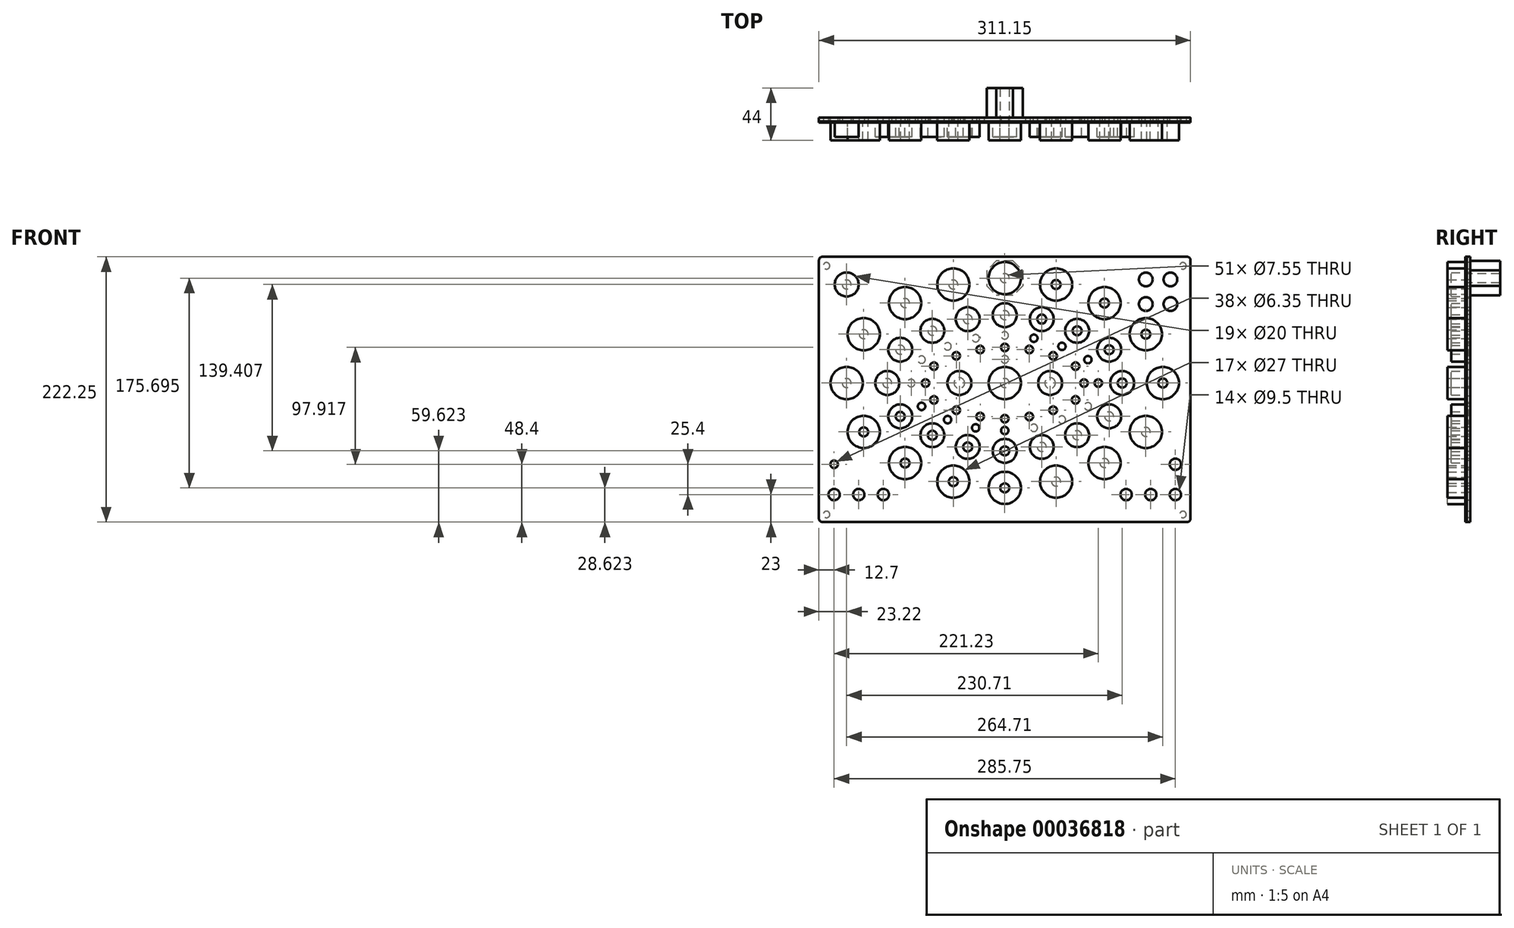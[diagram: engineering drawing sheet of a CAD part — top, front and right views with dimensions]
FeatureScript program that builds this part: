
annotation { "Feature Type Name" : "Feature", "Feature Type Description" : "" }
export const myFeature = defineFeature(function(context is Context, id is Id, definition is map)
    precondition{}
    {
        {
            var Q0;
            Q0=qCreatedBy(makeId("Front.planeOp"),FACE);
            var sketch = newSketch(context, id + "F0", { "sketchPlane" : qUnion([Q0])});
            skLineSegment(sketch, "E0.bottom", {"start": v(0, 0) * mm, "end": v(311.15, 0) * mm});
            skLineSegment(sketch, "E0.top", {"start": v(0, 222.25) * mm, "end": v(311.15, 222.25) * mm});
            skLineSegment(sketch, "E0.left", {"start": v(0, 0) * mm, "end": v(0, 222.25) * mm});
            skLineSegment(sketch, "E0.right", {"start": v(311.15, 0) * mm, "end": v(311.15, 222.25) * mm});
            skLineSegment(sketch, "E1", {"start": v(155.57, 222.25) * mm, "end": v(155.57, 0) * mm, "construction": true});
            skLineSegment(sketch, "E2", {"start": v(0, 116.47) * mm, "end": v(311.15, 116.47) * mm, "construction": true});
            skArc(sketch, "E3", {"start": v(50, 169.56) * mm, "mid": v(23.22, 116.47) * mm, "end": v(50, 63.38) * mm, "construction": true});
            skArc(sketch, "E4", {"start": v(261.14, 63.38) * mm, "mid": v(287.93, 116.47) * mm, "end": v(261.14, 169.56) * mm, "construction": true});
            skArc(sketch, "E5", {"start": v(50, 63.38) * mm, "mid": v(155.57, 28.62) * mm, "end": v(261.14, 63.38) * mm, "construction": true});
            skArc(sketch, "E6.trimOffspring", {"start": v(261.14, 169.56) * mm, "mid": v(155.57, 204.32) * mm, "end": v(50, 169.56) * mm, "construction": true});
            skPoint(sketch, "E7", {"position": v(23.22, 116.47) * mm});
            skPoint(sketch, "E8", {"position": v(287.93, 116.47) * mm});
            skPoint(sketch, "E9", {"position": v(155.57, 204.32) * mm});
            skPoint(sketch, "E10", {"position": v(155.57, 28.62) * mm});
            skLineSegment(sketch, "E11", {"start": v(23.22, 116.47) * mm, "end": v(37.45, 157.41) * mm, "construction": true});
            skLineSegment(sketch, "E12", {"start": v(72.09, 183.48) * mm, "end": v(37.45, 157.41) * mm, "construction": true});
            skLineSegment(sketch, "E13", {"start": v(72.09, 183.48) * mm, "end": v(112.55, 199.03) * mm, "construction": true});
            skLineSegment(sketch, "E14", {"start": v(155.57, 204.32) * mm, "end": v(112.55, 199.03) * mm, "construction": true});
            skLineSegment(sketch, "E15", {"start": v(112.55, 199.03) * mm, "end": v(72.09, 183.48) * mm, "construction": true});
            skCircle(sketch, "E16", {"center": v(23.22, 116.47) * mm, "radius": 3.78 * mm});
            skCircle(sketch, "E17", {"center": v(37.45, 157.41) * mm, "radius": 3.78 * mm});
            skCircle(sketch, "E18", {"center": v(72.09, 183.48) * mm, "radius": 3.78 * mm});
            skCircle(sketch, "E19", {"center": v(112.55, 199.03) * mm, "radius": 3.78 * mm});
            skCircle(sketch, "E20", {"center": v(155.57, 204.32) * mm, "radius": 3.78 * mm});
            skArc(sketch, "E21", {"start": v(242.72, 88.32) * mm, "mid": v(256.93, 116.47) * mm, "end": v(242.72, 144.62) * mm, "construction": true});
            skArc(sketch, "E22.trimOffspring", {"start": v(68.43, 144.62) * mm, "mid": v(54.22, 116.47) * mm, "end": v(68.43, 88.32) * mm, "construction": true});
            skArc(sketch, "E23.trimOffspring", {"start": v(242.72, 144.62) * mm, "mid": v(155.57, 173.32) * mm, "end": v(68.43, 144.62) * mm, "construction": true});
            skCircle(sketch, "E24", {"center": v(155.57, 173.32) * mm, "radius": 3.78 * mm});
            skCircle(sketch, "E25", {"center": v(124.57, 170) * mm, "radius": 3.78 * mm});
            skCircle(sketch, "E26", {"center": v(94.97, 160.21) * mm, "radius": 3.78 * mm});
            skArc(sketch, "E27", {"start": v(78.53, 130.95) * mm, "mid": v(71.22, 116.47) * mm, "end": v(78.53, 102) * mm, "construction": true});
            skArc(sketch, "E28", {"start": v(232.62, 102) * mm, "mid": v(239.93, 116.47) * mm, "end": v(232.62, 130.95) * mm, "construction": true});
            skArc(sketch, "E29.trimOffspring", {"start": v(232.62, 130.95) * mm, "mid": v(155.57, 156.32) * mm, "end": v(78.53, 130.95) * mm, "construction": true});
            skCircle(sketch, "E30", {"center": v(155.57, 156.32) * mm, "radius": 3.1 * mm});
            skCircle(sketch, "E31", {"center": v(131.21, 154) * mm, "radius": 3.1 * mm});
            skCircle(sketch, "E32", {"center": v(107.72, 147.16) * mm, "radius": 3.1 * mm});
            skLineSegment(sketch, "E33", {"start": v(107.72, 147.16) * mm, "end": v(131.21, 154) * mm, "construction": true});
            skLineSegment(sketch, "E34", {"start": v(131.21, 154) * mm, "end": v(155.57, 156.32) * mm, "construction": true});
            skLineSegment(sketch, "E35", {"start": v(94.97, 160.21) * mm, "end": v(124.57, 170) * mm, "construction": true});
            skLineSegment(sketch, "E36", {"start": v(124.57, 170) * mm, "end": v(155.57, 173.32) * mm, "construction": true});
            skCircle(sketch, "E37", {"center": v(54.22, 116.47) * mm, "radius": 3.78 * mm, "construction": true});
            skLineSegment(sketch, "E38", {"start": v(54.22, 116.47) * mm, "end": v(68.1, 144.39) * mm, "construction": true});
            skPoint(sketch, "E39.trimOffspring.end.orphan", {"position": v(311.15, 111.12) * mm});
            skArc(sketch, "E40", {"start": v(68.43, 88.32) * mm, "mid": v(155.57, 59.62) * mm, "end": v(242.72, 88.32) * mm, "construction": true});
            skArc(sketch, "E41", {"start": v(78.53, 102) * mm, "mid": v(155.57, 76.62) * mm, "end": v(232.62, 102) * mm, "construction": true});
            skCircle(sketch, "E42", {"center": v(71.22, 116.47) * mm, "radius": 3.1 * mm, "construction": true});
            skArc(sketch, "E43", {"start": v(84.47, 122.9) * mm, "mid": v(81.22, 116.47) * mm, "end": v(84.47, 110.03) * mm, "construction": true});
            skArc(sketch, "E44", {"start": v(226.68, 110.03) * mm, "mid": v(229.93, 116.47) * mm, "end": v(226.68, 122.9) * mm, "construction": true});
            skArc(sketch, "E45", {"start": v(226.68, 122.9) * mm, "mid": v(155.57, 146.32) * mm, "end": v(84.47, 122.9) * mm, "construction": true});
            skArc(sketch, "E46", {"start": v(84.47, 110.03) * mm, "mid": v(155.58, 86.62) * mm, "end": v(226.68, 110.03) * mm, "construction": true});
            skCircle(sketch, "E47", {"center": v(155.58, 146.32) * mm, "radius": 3.17 * mm});
            skCircle(sketch, "E48", {"center": v(81.22, 116.47) * mm, "radius": 3.17 * mm, "construction": true});
            skCircle(sketch, "E49", {"center": v(96.28, 130.6) * mm, "radius": 3.17 * mm});
            skCircle(sketch, "E50", {"center": v(115.04, 139.24) * mm, "radius": 3.17 * mm});
            skCircle(sketch, "E51", {"center": v(135, 144.54) * mm, "radius": 3.17 * mm});
            skLineSegment(sketch, "E52", {"start": v(155.58, 146.32) * mm, "end": v(135, 144.54) * mm, "construction": true});
            skLineSegment(sketch, "E53", {"start": v(135, 144.54) * mm, "end": v(115.04, 139.24) * mm, "construction": true});
            skLineSegment(sketch, "E54", {"start": v(115.04, 139.24) * mm, "end": v(96.28, 130.6) * mm, "construction": true});
            skLineSegment(sketch, "E55", {"start": v(96.28, 130.6) * mm, "end": v(81.22, 116.47) * mm, "construction": true});
            skLineSegment(sketch, "E56", {"start": v(68.1, 144.39) * mm, "end": v(94.97, 160.21) * mm, "construction": true});
            skCircle(sketch, "E57", {"center": v(68.1, 144.39) * mm, "radius": 3.78 * mm});
            skCircle(sketch, "E58", {"center": v(85.93, 136.03) * mm, "radius": 3.1 * mm});
            skLineSegment(sketch, "E59", {"start": v(71.22, 116.47) * mm, "end": v(85.93, 136.03) * mm, "construction": true});
            skLineSegment(sketch, "E60", {"start": v(107.72, 147.16) * mm, "end": v(85.93, 136.03) * mm, "construction": true});
            skCircle(sketch, "E61", {"center": v(117.57, 116.47) * mm, "radius": 4.45 * mm});
            skCircle(sketch, "E62", {"center": v(193.57, 116.47) * mm, "radius": 4.45 * mm});
            skCircle(sketch, "E63", {"center": v(155.58, 116.47) * mm, "radius": 3.78 * mm});
            skCircle(sketch, "E64", {"center": v(298.45, 23) * mm, "radius": 4.75 * mm});
            skCircle(sketch, "E65", {"center": v(298.45, 48.4) * mm, "radius": 4.75 * mm});
            skCircle(sketch, "E66", {"center": v(277.83, 23) * mm, "radius": 4.75 * mm});
            skCircle(sketch, "E67", {"center": v(257.2, 23) * mm, "radius": 4.75 * mm});
            skLineSegment(sketch, "E68", {"start": v(257.2, 23) * mm, "end": v(277.83, 23) * mm, "construction": true});
            skLineSegment(sketch, "E69", {"start": v(277.83, 23) * mm, "end": v(298.45, 23) * mm, "construction": true});
            skCircle(sketch, "E70.MirrorC", {"center": v(256.93, 116.47) * mm, "radius": 3.78 * mm, "construction": true});
            skCircle(sketch, "E71.MirrorC", {"center": v(243.04, 144.39) * mm, "radius": 3.78 * mm});
            skCircle(sketch, "E72.MirrorC", {"center": v(216.18, 160.21) * mm, "radius": 3.78 * mm});
            skCircle(sketch, "E73.MirrorC", {"center": v(186.58, 170) * mm, "radius": 3.78 * mm});
            skCircle(sketch, "E74.MirrorC", {"center": v(198.6, 199.03) * mm, "radius": 3.78 * mm});
            skCircle(sketch, "E75.MirrorC", {"center": v(239.06, 183.48) * mm, "radius": 3.78 * mm});
            skCircle(sketch, "E76.MirrorC", {"center": v(273.7, 157.41) * mm, "radius": 3.78 * mm});
            skCircle(sketch, "E77.MirrorC", {"center": v(287.93, 116.47) * mm, "radius": 3.78 * mm});
            skCircle(sketch, "E78.MirrorC", {"center": v(37.45, 75.53) * mm, "radius": 3.78 * mm});
            skCircle(sketch, "E79.MirrorC", {"center": v(72.09, 49.46) * mm, "radius": 3.78 * mm});
            skCircle(sketch, "E80.MirrorC", {"center": v(112.55, 33.9) * mm, "radius": 3.78 * mm});
            skCircle(sketch, "E81.MirrorC", {"center": v(155.57, 28.62) * mm, "radius": 3.78 * mm});
            skCircle(sketch, "E82.MirrorC", {"center": v(198.6, 33.9) * mm, "radius": 3.78 * mm});
            skCircle(sketch, "E83.MirrorC", {"center": v(239.06, 49.46) * mm, "radius": 3.78 * mm});
            skCircle(sketch, "E84.MirrorC", {"center": v(273.7, 75.53) * mm, "radius": 3.78 * mm});
            skCircle(sketch, "E85.MirrorC", {"center": v(243.04, 88.55) * mm, "radius": 3.78 * mm});
            skCircle(sketch, "E86.MirrorC", {"center": v(216.18, 72.73) * mm, "radius": 3.78 * mm});
            skCircle(sketch, "E87.MirrorC", {"center": v(186.58, 62.94) * mm, "radius": 3.78 * mm});
            skCircle(sketch, "E88.MirrorC", {"center": v(155.57, 59.62) * mm, "radius": 3.78 * mm});
            skCircle(sketch, "E89.MirrorC", {"center": v(124.57, 62.94) * mm, "radius": 3.78 * mm});
            skCircle(sketch, "E90.MirrorC", {"center": v(94.97, 72.73) * mm, "radius": 3.78 * mm});
            skCircle(sketch, "E91.MirrorC", {"center": v(68.1, 88.55) * mm, "radius": 3.78 * mm});
            skCircle(sketch, "E92.MirrorC", {"center": v(85.93, 96.91) * mm, "radius": 3.1 * mm});
            skCircle(sketch, "E93.MirrorC", {"center": v(107.72, 85.78) * mm, "radius": 3.1 * mm});
            skCircle(sketch, "E94.MirrorC", {"center": v(131.21, 78.93) * mm, "radius": 3.1 * mm});
            skCircle(sketch, "E95.MirrorC", {"center": v(155.57, 76.62) * mm, "radius": 3.1 * mm});
            skCircle(sketch, "E96.MirrorC", {"center": v(155.58, 86.62) * mm, "radius": 3.17 * mm});
            skCircle(sketch, "E97.MirrorC", {"center": v(135, 88.4) * mm, "radius": 3.17 * mm});
            skCircle(sketch, "E98.MirrorC", {"center": v(115.04, 93.7) * mm, "radius": 3.17 * mm});
            skCircle(sketch, "E99.MirrorC", {"center": v(96.28, 102.34) * mm, "radius": 3.17 * mm});
            skCircle(sketch, "E100.MirrorC", {"center": v(176.15, 144.54) * mm, "radius": 3.17 * mm});
            skCircle(sketch, "E101.MirrorC", {"center": v(179.94, 154) * mm, "radius": 3.1 * mm});
            skCircle(sketch, "E102.MirrorC", {"center": v(203.43, 147.16) * mm, "radius": 3.1 * mm});
            skCircle(sketch, "E103.MirrorC", {"center": v(196.11, 139.24) * mm, "radius": 3.17 * mm});
            skCircle(sketch, "E104.MirrorC", {"center": v(214.87, 130.6) * mm, "radius": 3.17 * mm});
            skCircle(sketch, "E105.MirrorC", {"center": v(225.22, 136.03) * mm, "radius": 3.1 * mm});
            skCircle(sketch, "E106.MirrorC", {"center": v(225.22, 96.91) * mm, "radius": 3.1 * mm});
            skCircle(sketch, "E107.MirrorC", {"center": v(203.43, 85.78) * mm, "radius": 3.1 * mm});
            skCircle(sketch, "E108.MirrorC", {"center": v(196.11, 93.7) * mm, "radius": 3.17 * mm});
            skCircle(sketch, "E109.MirrorC", {"center": v(176.15, 88.4) * mm, "radius": 3.17 * mm});
            skCircle(sketch, "E110.MirrorC", {"center": v(179.94, 78.93) * mm, "radius": 3.1 * mm});
            skCircle(sketch, "E111.MirrorC", {"center": v(239.93, 116.47) * mm, "radius": 3.1 * mm, "construction": true});
            skCircle(sketch, "E112.MirrorC", {"center": v(229.93, 116.47) * mm, "radius": 3.17 * mm, "construction": true});
            skCircle(sketch, "E113.MirrorC", {"center": v(33.32, 23) * mm, "radius": 4.75 * mm});
            skCircle(sketch, "E114.MirrorC", {"center": v(12.7, 23) * mm, "radius": 4.75 * mm});
            skCircle(sketch, "E115.MirrorC", {"center": v(12.7, 48.4) * mm, "radius": 4.75 * mm, "construction": true});
            skCircle(sketch, "E116.MirrorC", {"center": v(214.87, 102.34) * mm, "radius": 3.17 * mm});
            skCircle(sketch, "E117", {"center": v(89.22, 116.47) * mm, "radius": 3.17 * mm});
            skCircle(sketch, "E118", {"center": v(221.93, 116.47) * mm, "radius": 3.17 * mm});
            skCircle(sketch, "E119", {"center": v(294.32, 203.2) * mm, "radius": 5.75 * mm});
            skCircle(sketch, "E120", {"center": v(294.32, 182.58) * mm, "radius": 5.75 * mm});
            skCircle(sketch, "E121", {"center": v(273.7, 203.2) * mm, "radius": 5.75 * mm});
            skCircle(sketch, "E122", {"center": v(273.7, 182.58) * mm, "radius": 5.75 * mm});
            skCircle(sketch, "E123", {"center": v(23.22, 199.03) * mm, "radius": 3.78 * mm});
            skCircle(sketch, "E124", {"center": v(12.7, 48.4) * mm, "radius": 3.17 * mm});
            skCircle(sketch, "E125", {"center": v(155.58, 136.32) * mm, "radius": 3.17 * mm});
            skCircle(sketch, "E126", {"center": v(53.94, 23) * mm, "radius": 4.75 * mm});
            skCircle(sketch, "E127", {"center": v(236.59, 23) * mm, "radius": 4.75 * mm, "construction": true});
            skLineSegment(sketch, "E128", {"start": v(257.2, 23) * mm, "end": v(236.59, 23) * mm, "construction": true});
            skLineSegment(sketch, "E129", {"start": v(33.32, 23) * mm, "end": v(53.94, 23) * mm, "construction": true});
            skLineSegment(sketch, "E130", {"start": v(12.7, 23) * mm, "end": v(33.32, 23) * mm, "construction": true});
            skCircle(sketch, "E131", {"center": v(277.83, 48.4) * mm, "radius": 4.75 * mm, "construction": true});
            skCircle(sketch, "E132", {"center": v(77.22, 116.47) * mm, "radius": 3.17 * mm});
            skCircle(sketch, "E133", {"center": v(233.93, 116.47) * mm, "radius": 3.17 * mm});
            skLineSegment(sketch, "E134", {"start": v(273.7, 203.2) * mm, "end": v(294.32, 203.2) * mm, "construction": true});
            skCircle(sketch, "E135", {"center": v(273.7, 203.2) * mm, "radius": 6.5 * mm, "construction": true});
            skCircle(sketch, "E136", {"center": v(294.32, 203.2) * mm, "radius": 6.5 * mm, "construction": true});
            skCircle(sketch, "E137", {"center": v(294.32, 182.58) * mm, "radius": 6.5 * mm, "construction": true});
            skCircle(sketch, "E138", {"center": v(273.7, 182.58) * mm, "radius": 6.5 * mm, "construction": true});
            skLineSegment(sketch, "E139", {"start": v(273.7, 203.2) * mm, "end": v(273.7, 194.14) * mm, "construction": true});
            skLineSegment(sketch, "E140", {"start": v(273.7, 194.14) * mm, "end": v(273.7, 191.64) * mm});
            skLineSegment(sketch, "E141", {"start": v(273.7, 191.64) * mm, "end": v(273.7, 182.58) * mm, "construction": true});
            skCircle(sketch, "E142", {"center": v(57.22, 116.47) * mm, "radius": 3.78 * mm});
            skCircle(sketch, "E143.MirrorC", {"center": v(253.93, 116.47) * mm, "radius": 3.78 * mm});
            skSolve(sketch);
        }
        {
            var Q0;
            Q0=makeQuery(id+"F0.imprint","IMPRINT",FACE,{"disambiguationData":[TD([[makeQuery(id+"F0.imprint","IMPRINT",EDGE,{"derivedFrom":sQuery(id+"F0.wireOp",EDGE,"E0.bottom")}),1.0]])]});
            extrude(context, id + "F1", {"entities" : qUnion([Q0]), "oppositeDirection" : true, "depth" : 3 * mm});
        }
        {
            var Q0;
            Q0=makeQuery(id+"F1.opExtrude","SWEPT_EDGE",EDGE,{"disambiguationData":[OSD([sQuery(id+"F0.wireOp",EDGE,"E0.top"),sQuery(id+"F0.wireOp",EDGE,"E0.left")])]});
            var Q1;
            Q1=makeQuery(id+"F1.opExtrude","SWEPT_EDGE",EDGE,{"disambiguationData":[OSD([sQuery(id+"F0.wireOp",EDGE,"E0.bottom"),sQuery(id+"F0.wireOp",EDGE,"E0.left")])]});
            var Q2;
            Q2=makeQuery(id+"F1.opExtrude","SWEPT_EDGE",EDGE,{"disambiguationData":[OSD([sQuery(id+"F0.wireOp",EDGE,"E0.top"),sQuery(id+"F0.wireOp",EDGE,"E0.right")])]});
            var Q3;
            Q3=makeQuery(id+"F1.opExtrude","SWEPT_EDGE",EDGE,{"disambiguationData":[OSD([sQuery(id+"F0.wireOp",EDGE,"E0.bottom"),sQuery(id+"F0.wireOp",EDGE,"E0.right")])]});
            fillet(context, id + "F2", {"entities" : qUnion([Q0, Q1, Q2, Q3]), "radius" : 3 * mm, "tangentPropagation" : true, "allowEdgeOverflow" : false});
        }
        {
            var Q0;
            Q0=makeQuery(id+"F1.opExtrude","CAP_FACE",FACE,{"disambiguationData":[OSD([sQuery(id+"F0.wireOp",EDGE,"E0.bottom"),sQuery(id+"F0.wireOp",EDGE,"E0.top"),sQuery(id+"F0.wireOp",EDGE,"E0.left"),sQuery(id+"F0.wireOp",EDGE,"E0.right"),sQuery(id+"F0.wireOp",EDGE,"E16"),sQuery(id+"F0.wireOp",EDGE,"E17"),sQuery(id+"F0.wireOp",EDGE,"E18"),sQuery(id+"F0.wireOp",EDGE,"E19"),sQuery(id+"F0.wireOp",EDGE,"E20"),sQuery(id+"F0.wireOp",EDGE,"E24"),sQuery(id+"F0.wireOp",EDGE,"E25"),sQuery(id+"F0.wireOp",EDGE,"E26"),sQuery(id+"F0.wireOp",EDGE,"E30"),sQuery(id+"F0.wireOp",EDGE,"E31"),sQuery(id+"F0.wireOp",EDGE,"E32"),sQuery(id+"F0.wireOp",EDGE,"E37"),sQuery(id+"F0.wireOp",EDGE,"E42"),sQuery(id+"F0.wireOp",EDGE,"E47"),sQuery(id+"F0.wireOp",EDGE,"E49"),sQuery(id+"F0.wireOp",EDGE,"E50"),sQuery(id+"F0.wireOp",EDGE,"E51"),sQuery(id+"F0.wireOp",EDGE,"E57"),sQuery(id+"F0.wireOp",EDGE,"E58"),sQuery(id+"F0.wireOp",EDGE,"E61"),sQuery(id+"F0.wireOp",EDGE,"E62"),sQuery(id+"F0.wireOp",EDGE,"E63"),sQuery(id+"F0.wireOp",EDGE,"E64"),sQuery(id+"F0.wireOp",EDGE,"E65"),sQuery(id+"F0.wireOp",EDGE,"E66"),sQuery(id+"F0.wireOp",EDGE,"E67"),sQuery(id+"F0.wireOp",EDGE,"E70.MirrorC"),sQuery(id+"F0.wireOp",EDGE,"E71.MirrorC"),sQuery(id+"F0.wireOp",EDGE,"E72.MirrorC"),sQuery(id+"F0.wireOp",EDGE,"E73.MirrorC"),sQuery(id+"F0.wireOp",EDGE,"E74.MirrorC"),sQuery(id+"F0.wireOp",EDGE,"E75.MirrorC"),sQuery(id+"F0.wireOp",EDGE,"E77.MirrorC"),sQuery(id+"F0.wireOp",EDGE,"E76.MirrorC"),sQuery(id+"F0.wireOp",EDGE,"E78.MirrorC"),sQuery(id+"F0.wireOp",EDGE,"E79.MirrorC"),sQuery(id+"F0.wireOp",EDGE,"E80.MirrorC"),sQuery(id+"F0.wireOp",EDGE,"E81.MirrorC"),sQuery(id+"F0.wireOp",EDGE,"E82.MirrorC"),sQuery(id+"F0.wireOp",EDGE,"E83.MirrorC"),sQuery(id+"F0.wireOp",EDGE,"E84.MirrorC"),sQuery(id+"F0.wireOp",EDGE,"E85.MirrorC"),sQuery(id+"F0.wireOp",EDGE,"E86.MirrorC"),sQuery(id+"F0.wireOp",EDGE,"E87.MirrorC"),sQuery(id+"F0.wireOp",EDGE,"E88.MirrorC"),sQuery(id+"F0.wireOp",EDGE,"E89.MirrorC"),sQuery(id+"F0.wireOp",EDGE,"E90.MirrorC"),sQuery(id+"F0.wireOp",EDGE,"E91.MirrorC"),sQuery(id+"F0.wireOp",EDGE,"E92.MirrorC"),sQuery(id+"F0.wireOp",EDGE,"E93.MirrorC"),sQuery(id+"F0.wireOp",EDGE,"E94.MirrorC"),sQuery(id+"F0.wireOp",EDGE,"E95.MirrorC"),sQuery(id+"F0.wireOp",EDGE,"E96.MirrorC"),sQuery(id+"F0.wireOp",EDGE,"E97.MirrorC"),sQuery(id+"F0.wireOp",EDGE,"E98.MirrorC"),sQuery(id+"F0.wireOp",EDGE,"E99.MirrorC"),sQuery(id+"F0.wireOp",EDGE,"E100.MirrorC"),sQuery(id+"F0.wireOp",EDGE,"E101.MirrorC"),sQuery(id+"F0.wireOp",EDGE,"E102.MirrorC"),sQuery(id+"F0.wireOp",EDGE,"E103.MirrorC"),sQuery(id+"F0.wireOp",EDGE,"E104.MirrorC"),sQuery(id+"F0.wireOp",EDGE,"E105.MirrorC"),sQuery(id+"F0.wireOp",EDGE,"E106.MirrorC"),sQuery(id+"F0.wireOp",EDGE,"E107.MirrorC"),sQuery(id+"F0.wireOp",EDGE,"E108.MirrorC"),sQuery(id+"F0.wireOp",EDGE,"E109.MirrorC"),sQuery(id+"F0.wireOp",EDGE,"E110.MirrorC"),sQuery(id+"F0.wireOp",EDGE,"E111.MirrorC"),sQuery(id+"F0.wireOp",EDGE,"E113.MirrorC"),sQuery(id+"F0.wireOp",EDGE,"E114.MirrorC"),sQuery(id+"F0.wireOp",EDGE,"E115.MirrorC"),sQuery(id+"F0.wireOp",EDGE,"E116.MirrorC"),sQuery(id+"F0.wireOp",EDGE,"E117"),sQuery(id+"F0.wireOp",EDGE,"E118"),sQuery(id+"F0.wireOp",EDGE,"E119"),sQuery(id+"F0.wireOp",EDGE,"E120"),sQuery(id+"F0.wireOp",EDGE,"E121"),sQuery(id+"F0.wireOp",EDGE,"E122"),sQuery(id+"F0.wireOp",EDGE,"E123"),sQuery(id+"F0.wireOp",EDGE,"E124"),sQuery(id+"F0.wireOp",EDGE,"E125")])],"isStart":true});
            var sketch = newSketch(context, id + "F3", { "sketchPlane" : qUnion([Q0])});
            skCircle(sketch, "E144.0", {"center": v(37.45, 157.41) * mm, "radius": 3.78 * mm, "construction": true});
            skCircle(sketch, "E145.0", {"center": v(23.22, 199.03) * mm, "radius": 3.78 * mm, "construction": true});
            skCircle(sketch, "E146.0", {"center": v(12.7, 48.4) * mm, "radius": 3.17 * mm, "construction": true});
            skCircle(sketch, "E147.0", {"center": v(155.58, 136.32) * mm, "radius": 3.17 * mm, "construction": true});
            skCircle(sketch, "E148.0", {"center": v(72.09, 183.48) * mm, "radius": 3.78 * mm, "construction": true});
            skCircle(sketch, "E149.0", {"center": v(68.1, 144.39) * mm, "radius": 3.78 * mm, "construction": true});
            skCircle(sketch, "E150.0", {"center": v(57.22, 116.47) * mm, "radius": 3.78 * mm, "construction": true});
            skCircle(sketch, "E151.0", {"center": v(23.22, 116.47) * mm, "radius": 3.78 * mm, "construction": true});
            skCircle(sketch, "E152.0", {"center": v(37.45, 75.53) * mm, "radius": 3.78 * mm, "construction": true});
            skCircle(sketch, "E153.0", {"center": v(12.7, 23) * mm, "radius": 4.75 * mm, "construction": true});
            skCircle(sketch, "E154.0", {"center": v(33.32, 23) * mm, "radius": 4.75 * mm, "construction": true});
            skCircle(sketch, "E155.0", {"center": v(72.09, 49.46) * mm, "radius": 3.78 * mm, "construction": true});
            skCircle(sketch, "E156.0", {"center": v(112.55, 33.9) * mm, "radius": 3.78 * mm, "construction": true});
            skCircle(sketch, "E157.0", {"center": v(94.97, 72.73) * mm, "radius": 3.78 * mm, "construction": true});
            skCircle(sketch, "E158.0", {"center": v(68.1, 88.55) * mm, "radius": 3.78 * mm, "construction": true});
            skCircle(sketch, "E159.0", {"center": v(85.93, 96.91) * mm, "radius": 3.1 * mm, "construction": true});
            skCircle(sketch, "E160.0", {"center": v(89.22, 116.47) * mm, "radius": 3.17 * mm, "construction": true});
            skCircle(sketch, "E161.0", {"center": v(85.93, 136.03) * mm, "radius": 3.1 * mm, "construction": true});
            skCircle(sketch, "E162.0", {"center": v(94.97, 160.21) * mm, "radius": 3.78 * mm, "construction": true});
            skCircle(sketch, "E163.0", {"center": v(96.28, 130.6) * mm, "radius": 3.17 * mm, "construction": true});
            skCircle(sketch, "E164.0", {"center": v(107.72, 147.16) * mm, "radius": 3.1 * mm, "construction": true});
            skCircle(sketch, "E165.0", {"center": v(115.04, 139.24) * mm, "radius": 3.17 * mm, "construction": true});
            skCircle(sketch, "E166.0", {"center": v(96.28, 102.34) * mm, "radius": 3.17 * mm, "construction": true});
            skCircle(sketch, "E167.0", {"center": v(117.57, 116.47) * mm, "radius": 4.45 * mm, "construction": true});
            skCircle(sketch, "E168.0", {"center": v(115.04, 93.7) * mm, "radius": 3.17 * mm, "construction": true});
            skCircle(sketch, "E169.0", {"center": v(107.72, 85.78) * mm, "radius": 3.1 * mm, "construction": true});
            skCircle(sketch, "E170.0", {"center": v(124.57, 62.94) * mm, "radius": 3.78 * mm, "construction": true});
            skCircle(sketch, "E171.0", {"center": v(131.21, 78.93) * mm, "radius": 3.1 * mm, "construction": true});
            skCircle(sketch, "E172.0", {"center": v(135, 88.4) * mm, "radius": 3.17 * mm, "construction": true});
            skCircle(sketch, "E173.0", {"center": v(135, 144.54) * mm, "radius": 3.17 * mm, "construction": true});
            skCircle(sketch, "E174.0", {"center": v(131.21, 154) * mm, "radius": 3.1 * mm, "construction": true});
            skCircle(sketch, "E175.0", {"center": v(124.57, 170) * mm, "radius": 3.78 * mm, "construction": true});
            skCircle(sketch, "E176.0", {"center": v(112.55, 199.03) * mm, "radius": 3.78 * mm, "construction": true});
            skCircle(sketch, "E177.0", {"center": v(155.57, 204.32) * mm, "radius": 3.78 * mm, "construction": true});
            skCircle(sketch, "E178.0", {"center": v(155.57, 173.32) * mm, "radius": 3.78 * mm, "construction": true});
            skCircle(sketch, "E179.0", {"center": v(155.57, 156.32) * mm, "radius": 3.1 * mm, "construction": true});
            skCircle(sketch, "E180.0", {"center": v(155.58, 146.32) * mm, "radius": 3.17 * mm, "construction": true});
            skCircle(sketch, "E181.0", {"center": v(155.58, 116.47) * mm, "radius": 3.78 * mm, "construction": true});
            skCircle(sketch, "E182.0", {"center": v(155.58, 86.62) * mm, "radius": 3.17 * mm, "construction": true});
            skCircle(sketch, "E183.0", {"center": v(155.57, 76.62) * mm, "radius": 3.1 * mm, "construction": true});
            skCircle(sketch, "E184.0", {"center": v(155.57, 59.62) * mm, "radius": 3.78 * mm, "construction": true});
            skCircle(sketch, "E185.0", {"center": v(155.57, 28.62) * mm, "radius": 3.78 * mm, "construction": true});
            skCircle(sketch, "E186.0", {"center": v(198.6, 33.9) * mm, "radius": 3.78 * mm, "construction": true});
            skCircle(sketch, "E187.0", {"center": v(186.58, 62.94) * mm, "radius": 3.78 * mm, "construction": true});
            skCircle(sketch, "E188.0", {"center": v(179.94, 78.93) * mm, "radius": 3.1 * mm, "construction": true});
            skCircle(sketch, "E189.0", {"center": v(176.15, 88.4) * mm, "radius": 3.17 * mm, "construction": true});
            skCircle(sketch, "E190.0", {"center": v(196.11, 93.7) * mm, "radius": 3.17 * mm, "construction": true});
            skCircle(sketch, "E191.0", {"center": v(203.43, 85.78) * mm, "radius": 3.1 * mm, "construction": true});
            skCircle(sketch, "E192.0", {"center": v(216.18, 72.73) * mm, "radius": 3.78 * mm, "construction": true});
            skCircle(sketch, "E193.0", {"center": v(239.06, 49.46) * mm, "radius": 3.78 * mm, "construction": true});
            skCircle(sketch, "E194.0", {"center": v(277.83, 23) * mm, "radius": 4.75 * mm, "construction": true});
            skCircle(sketch, "E195.0", {"center": v(298.45, 23) * mm, "radius": 4.75 * mm, "construction": true});
            skCircle(sketch, "E196.0", {"center": v(273.7, 75.53) * mm, "radius": 3.78 * mm, "construction": true});
            skCircle(sketch, "E197.0", {"center": v(243.04, 88.55) * mm, "radius": 3.78 * mm, "construction": true});
            skCircle(sketch, "E198.0", {"center": v(225.22, 96.91) * mm, "radius": 3.1 * mm, "construction": true});
            skCircle(sketch, "E199.0", {"center": v(214.87, 102.34) * mm, "radius": 3.17 * mm, "construction": true});
            skCircle(sketch, "E200.0", {"center": v(193.57, 116.47) * mm, "radius": 4.45 * mm, "construction": true});
            skCircle(sketch, "E201.0", {"center": v(214.87, 130.6) * mm, "radius": 3.17 * mm, "construction": true});
            skCircle(sketch, "E202.0", {"center": v(225.22, 136.03) * mm, "radius": 3.1 * mm, "construction": true});
            skCircle(sketch, "E203.0", {"center": v(243.04, 144.39) * mm, "radius": 3.78 * mm, "construction": true});
            skCircle(sketch, "E204.0", {"center": v(273.7, 157.41) * mm, "radius": 3.78 * mm, "construction": true});
            skCircle(sketch, "E205.0", {"center": v(239.06, 183.48) * mm, "radius": 3.78 * mm, "construction": true});
            skCircle(sketch, "E206.0", {"center": v(216.18, 160.21) * mm, "radius": 3.78 * mm, "construction": true});
            skCircle(sketch, "E207.0", {"center": v(203.43, 147.16) * mm, "radius": 3.1 * mm, "construction": true});
            skCircle(sketch, "E208.0", {"center": v(196.11, 139.24) * mm, "radius": 3.17 * mm, "construction": true});
            skCircle(sketch, "E209.0", {"center": v(176.15, 144.54) * mm, "radius": 3.17 * mm, "construction": true});
            skCircle(sketch, "E210.0", {"center": v(179.94, 154) * mm, "radius": 3.1 * mm, "construction": true});
            skCircle(sketch, "E211.0", {"center": v(186.58, 170) * mm, "radius": 3.78 * mm, "construction": true});
            skCircle(sketch, "E212.0", {"center": v(198.6, 199.03) * mm, "radius": 3.78 * mm, "construction": true});
            skCircle(sketch, "E213.0", {"center": v(221.93, 116.47) * mm, "radius": 3.17 * mm, "construction": true});
            skCircle(sketch, "E214.0", {"center": v(287.93, 116.47) * mm, "radius": 3.78 * mm, "construction": true});
            skCircle(sketch, "E215", {"center": v(72.09, 183.48) * mm, "radius": 13.5 * mm});
            skCircle(sketch, "E216", {"center": v(112.55, 199.03) * mm, "radius": 13.5 * mm});
            skCircle(sketch, "E217", {"center": v(155.57, 204.32) * mm, "radius": 13.5 * mm});
            skCircle(sketch, "E218", {"center": v(198.6, 199.03) * mm, "radius": 13.5 * mm});
            skCircle(sketch, "E219", {"center": v(37.45, 157.41) * mm, "radius": 13.5 * mm});
            skCircle(sketch, "E220", {"center": v(23.22, 116.47) * mm, "radius": 13.5 * mm});
            skCircle(sketch, "E221", {"center": v(37.45, 75.53) * mm, "radius": 13.5 * mm});
            skCircle(sketch, "E222", {"center": v(72.09, 49.46) * mm, "radius": 13.5 * mm});
            skCircle(sketch, "E223", {"center": v(155.57, 28.62) * mm, "radius": 13.5 * mm});
            skCircle(sketch, "E224", {"center": v(198.6, 33.9) * mm, "radius": 13.5 * mm});
            skCircle(sketch, "E225", {"center": v(239.06, 49.46) * mm, "radius": 13.5 * mm});
            skCircle(sketch, "E226", {"center": v(273.7, 75.53) * mm, "radius": 13.5 * mm});
            skCircle(sketch, "E227", {"center": v(287.93, 116.47) * mm, "radius": 13.5 * mm});
            skCircle(sketch, "E228", {"center": v(273.7, 157.41) * mm, "radius": 13.5 * mm});
            skCircle(sketch, "E229", {"center": v(239.06, 183.48) * mm, "radius": 13.5 * mm});
            skCircle(sketch, "E230", {"center": v(155.57, 116.47) * mm, "radius": 13.5 * mm});
            skCircle(sketch, "E231", {"center": v(112.55, 33.9) * mm, "radius": 13.5 * mm});
            skCircle(sketch, "E232", {"center": v(124.57, 170) * mm, "radius": 10 * mm});
            skCircle(sketch, "E233", {"center": v(155.57, 173.32) * mm, "radius": 10 * mm});
            skCircle(sketch, "E234", {"center": v(186.58, 170) * mm, "radius": 10 * mm});
            skCircle(sketch, "E235", {"center": v(216.18, 160.21) * mm, "radius": 10 * mm});
            skCircle(sketch, "E236", {"center": v(243.04, 144.39) * mm, "radius": 10 * mm});
            skCircle(sketch, "E237", {"center": v(57.22, 116.47) * mm, "radius": 10 * mm});
            skCircle(sketch, "E238", {"center": v(243.04, 88.55) * mm, "radius": 10 * mm});
            skCircle(sketch, "E239", {"center": v(94.97, 160.21) * mm, "radius": 10 * mm});
            skCircle(sketch, "E240", {"center": v(68.1, 144.39) * mm, "radius": 10 * mm});
            skCircle(sketch, "E241", {"center": v(68.1, 88.55) * mm, "radius": 10 * mm});
            skCircle(sketch, "E242", {"center": v(94.97, 72.73) * mm, "radius": 10 * mm});
            skCircle(sketch, "E243", {"center": v(155.57, 59.62) * mm, "radius": 10 * mm});
            skCircle(sketch, "E244", {"center": v(186.58, 62.94) * mm, "radius": 10 * mm});
            skCircle(sketch, "E245", {"center": v(216.18, 72.73) * mm, "radius": 10 * mm});
            skCircle(sketch, "E246", {"center": v(193.57, 116.47) * mm, "radius": 10 * mm});
            skCircle(sketch, "E247", {"center": v(117.57, 116.47) * mm, "radius": 10 * mm});
            skCircle(sketch, "E248", {"center": v(124.57, 62.94) * mm, "radius": 10 * mm});
            skCircle(sketch, "E249", {"center": v(23.22, 199.03) * mm, "radius": 10 * mm});
            skCircle(sketch, "E250.0", {"center": v(77.22, 116.47) * mm, "radius": 3.17 * mm});
            skCircle(sketch, "E251.0", {"center": v(233.93, 116.47) * mm, "radius": 3.1 * mm});
            skCircle(sketch, "E252", {"center": v(253.93, 116.47) * mm, "radius": 10 * mm});
            skSolve(sketch);
        }
        {
            var Q0;
            Q0=makeQuery(id+"F3.imprint","IMPRINT",FACE,{"disambiguationData":[TD([[makeQuery(id+"F3.imprint","IMPRINT",EDGE,{"derivedFrom":sQuery(id+"F3.wireOp",EDGE,"E240")}),1.0]])]});
            var Q1;
            Q1=makeQuery(id+"F3.imprint","IMPRINT",FACE,{"disambiguationData":[TD([[makeQuery(id+"F3.imprint","IMPRINT",EDGE,{"derivedFrom":makeQuery(id+"F1.opExtrude","CAP_EDGE",EDGE,{"disambiguationData":[OSD([sQuery(id+"F0.wireOp",EDGE,"E57")])],"isStart":true})}),1.0]])]});
            var Q2;
            Q2=makeQuery(id+"F3.imprint","IMPRINT",FACE,{"disambiguationData":[TD([[makeQuery(id+"F3.imprint","IMPRINT",EDGE,{"derivedFrom":makeQuery(id+"F1.opExtrude","CAP_EDGE",EDGE,{"disambiguationData":[OSD([sQuery(id+"F0.wireOp",EDGE,"E37")])],"isStart":true})}),1.0]])]});
            var Q3;
            Q3=makeQuery(id+"F3.imprint","IMPRINT",FACE,{"disambiguationData":[TD([[makeQuery(id+"F3.imprint","IMPRINT",EDGE,{"derivedFrom":sQuery(id+"F3.wireOp",EDGE,"E239")}),1.0]])]});
            var Q4;
            Q4=makeQuery(id+"F3.imprint","IMPRINT",FACE,{"disambiguationData":[TD([[makeQuery(id+"F3.imprint","IMPRINT",EDGE,{"derivedFrom":sQuery(id+"F3.wireOp",EDGE,"E232")}),1.0]])]});
            var Q5;
            Q5=makeQuery(id+"F3.imprint","IMPRINT",FACE,{"disambiguationData":[TD([[makeQuery(id+"F3.imprint","IMPRINT",EDGE,{"derivedFrom":makeQuery(id+"F1.opExtrude","CAP_EDGE",EDGE,{"disambiguationData":[OSD([sQuery(id+"F0.wireOp",EDGE,"E25")])],"isStart":true})}),1.0]])]});
            var Q6;
            Q6=makeQuery(id+"F3.imprint","IMPRINT",FACE,{"disambiguationData":[TD([[makeQuery(id+"F3.imprint","IMPRINT",EDGE,{"derivedFrom":makeQuery(id+"F1.opExtrude","CAP_EDGE",EDGE,{"disambiguationData":[OSD([sQuery(id+"F0.wireOp",EDGE,"E26")])],"isStart":true})}),1.0]])]});
            var Q7;
            Q7=makeQuery(id+"F3.imprint","IMPRINT",FACE,{"disambiguationData":[TD([[makeQuery(id+"F3.imprint","IMPRINT",EDGE,{"derivedFrom":sQuery(id+"F3.wireOp",EDGE,"E241")}),1.0]])]});
            var Q8;
            Q8=makeQuery(id+"F3.imprint","IMPRINT",FACE,{"disambiguationData":[TD([[makeQuery(id+"F3.imprint","IMPRINT",EDGE,{"derivedFrom":makeQuery(id+"F1.opExtrude","CAP_EDGE",EDGE,{"disambiguationData":[OSD([sQuery(id+"F0.wireOp",EDGE,"E91.MirrorC")])],"isStart":true})}),-1.0]])]});
            var Q9;
            Q9=makeQuery(id+"F3.imprint","IMPRINT",FACE,{"disambiguationData":[TD([[makeQuery(id+"F3.imprint","IMPRINT",EDGE,{"derivedFrom":sQuery(id+"F3.wireOp",EDGE,"E242")}),1.0]])]});
            var Q10;
            Q10=makeQuery(id+"F3.imprint","IMPRINT",FACE,{"disambiguationData":[TD([[makeQuery(id+"F3.imprint","IMPRINT",EDGE,{"derivedFrom":makeQuery(id+"F1.opExtrude","CAP_EDGE",EDGE,{"disambiguationData":[OSD([sQuery(id+"F0.wireOp",EDGE,"E90.MirrorC")])],"isStart":true})}),-1.0]])]});
            var Q11;
            Q11=makeQuery(id+"F3.imprint","IMPRINT",FACE,{"disambiguationData":[TD([[makeQuery(id+"F3.imprint","IMPRINT",EDGE,{"derivedFrom":sQuery(id+"F3.wireOp",EDGE,"E248")}),1.0]])]});
            var Q12;
            Q12=makeQuery(id+"F3.imprint","IMPRINT",FACE,{"disambiguationData":[TD([[makeQuery(id+"F3.imprint","IMPRINT",EDGE,{"derivedFrom":makeQuery(id+"F1.opExtrude","CAP_EDGE",EDGE,{"disambiguationData":[OSD([sQuery(id+"F0.wireOp",EDGE,"E89.MirrorC")])],"isStart":true})}),-1.0]])]});
            var Q13;
            Q13=makeQuery(id+"F3.imprint","IMPRINT",FACE,{"disambiguationData":[TD([[makeQuery(id+"F3.imprint","IMPRINT",EDGE,{"derivedFrom":sQuery(id+"F3.wireOp",EDGE,"E243")}),1.0]])]});
            var Q14;
            Q14=makeQuery(id+"F3.imprint","IMPRINT",FACE,{"disambiguationData":[TD([[makeQuery(id+"F3.imprint","IMPRINT",EDGE,{"derivedFrom":makeQuery(id+"F1.opExtrude","CAP_EDGE",EDGE,{"disambiguationData":[OSD([sQuery(id+"F0.wireOp",EDGE,"E88.MirrorC")])],"isStart":true})}),-1.0]])]});
            var Q15;
            Q15=makeQuery(id+"F3.imprint","IMPRINT",FACE,{"disambiguationData":[TD([[makeQuery(id+"F3.imprint","IMPRINT",EDGE,{"derivedFrom":sQuery(id+"F3.wireOp",EDGE,"E244")}),1.0]])]});
            var Q16;
            Q16=makeQuery(id+"F3.imprint","IMPRINT",FACE,{"disambiguationData":[TD([[makeQuery(id+"F3.imprint","IMPRINT",EDGE,{"derivedFrom":makeQuery(id+"F1.opExtrude","CAP_EDGE",EDGE,{"disambiguationData":[OSD([sQuery(id+"F0.wireOp",EDGE,"E87.MirrorC")])],"isStart":true})}),1.0]])]});
            var Q17;
            Q17=makeQuery(id+"F3.imprint","IMPRINT",FACE,{"disambiguationData":[TD([[makeQuery(id+"F3.imprint","IMPRINT",EDGE,{"derivedFrom":sQuery(id+"F3.wireOp",EDGE,"E245")}),1.0]])]});
            var Q18;
            Q18=makeQuery(id+"F3.imprint","IMPRINT",FACE,{"disambiguationData":[TD([[makeQuery(id+"F3.imprint","IMPRINT",EDGE,{"derivedFrom":makeQuery(id+"F1.opExtrude","CAP_EDGE",EDGE,{"disambiguationData":[OSD([sQuery(id+"F0.wireOp",EDGE,"E86.MirrorC")])],"isStart":true})}),1.0]])]});
            var Q19;
            Q19=makeQuery(id+"F3.imprint","IMPRINT",FACE,{"disambiguationData":[TD([[makeQuery(id+"F3.imprint","IMPRINT",EDGE,{"derivedFrom":sQuery(id+"F3.wireOp",EDGE,"E238")}),1.0]])]});
            var Q20;
            Q20=makeQuery(id+"F3.imprint","IMPRINT",FACE,{"disambiguationData":[TD([[makeQuery(id+"F3.imprint","IMPRINT",EDGE,{"derivedFrom":makeQuery(id+"F1.opExtrude","CAP_EDGE",EDGE,{"disambiguationData":[OSD([sQuery(id+"F0.wireOp",EDGE,"E85.MirrorC")])],"isStart":true})}),1.0]])]});
            var Q21;
            Q21=makeQuery(id+"F3.imprint","IMPRINT",FACE,{"disambiguationData":[TD([[makeQuery(id+"F3.imprint","IMPRINT",EDGE,{"derivedFrom":sQuery(id+"F3.wireOp",EDGE,"E237")}),1.0]])]});
            var Q22;
            Q22=makeQuery(id+"F3.imprint","IMPRINT",FACE,{"disambiguationData":[TD([[makeQuery(id+"F3.imprint","IMPRINT",EDGE,{"derivedFrom":makeQuery(id+"F1.opExtrude","CAP_EDGE",EDGE,{"disambiguationData":[OSD([sQuery(id+"F0.wireOp",EDGE,"E70.MirrorC")])],"isStart":true})}),-1.0]])]});
            var Q23;
            Q23=makeQuery(id+"F3.imprint","IMPRINT",FACE,{"disambiguationData":[TD([[makeQuery(id+"F3.imprint","IMPRINT",EDGE,{"derivedFrom":sQuery(id+"F3.wireOp",EDGE,"E236")}),1.0]])]});
            var Q24;
            Q24=makeQuery(id+"F3.imprint","IMPRINT",FACE,{"disambiguationData":[TD([[makeQuery(id+"F3.imprint","IMPRINT",EDGE,{"derivedFrom":makeQuery(id+"F1.opExtrude","CAP_EDGE",EDGE,{"disambiguationData":[OSD([sQuery(id+"F0.wireOp",EDGE,"E71.MirrorC")])],"isStart":true})}),-1.0]])]});
            var Q25;
            Q25=makeQuery(id+"F3.imprint","IMPRINT",FACE,{"disambiguationData":[TD([[makeQuery(id+"F3.imprint","IMPRINT",EDGE,{"derivedFrom":sQuery(id+"F3.wireOp",EDGE,"E235")}),1.0]])]});
            var Q26;
            Q26=makeQuery(id+"F3.imprint","IMPRINT",FACE,{"disambiguationData":[TD([[makeQuery(id+"F3.imprint","IMPRINT",EDGE,{"derivedFrom":makeQuery(id+"F1.opExtrude","CAP_EDGE",EDGE,{"disambiguationData":[OSD([sQuery(id+"F0.wireOp",EDGE,"E72.MirrorC")])],"isStart":true})}),-1.0]])]});
            var Q27;
            Q27=makeQuery(id+"F3.imprint","IMPRINT",FACE,{"disambiguationData":[TD([[makeQuery(id+"F3.imprint","IMPRINT",EDGE,{"derivedFrom":sQuery(id+"F3.wireOp",EDGE,"E234")}),1.0]])]});
            var Q28;
            Q28=makeQuery(id+"F3.imprint","IMPRINT",FACE,{"disambiguationData":[TD([[makeQuery(id+"F3.imprint","IMPRINT",EDGE,{"derivedFrom":makeQuery(id+"F1.opExtrude","CAP_EDGE",EDGE,{"disambiguationData":[OSD([sQuery(id+"F0.wireOp",EDGE,"E24")])],"isStart":true})}),1.0]])]});
            var Q29;
            Q29=makeQuery(id+"F3.imprint","IMPRINT",FACE,{"disambiguationData":[TD([[makeQuery(id+"F3.imprint","IMPRINT",EDGE,{"derivedFrom":sQuery(id+"F3.wireOp",EDGE,"E247")}),1.0]])]});
            var Q30;
            Q30=makeQuery(id+"F3.imprint","IMPRINT",FACE,{"disambiguationData":[TD([[makeQuery(id+"F3.imprint","IMPRINT",EDGE,{"derivedFrom":makeQuery(id+"F1.opExtrude","CAP_EDGE",EDGE,{"disambiguationData":[OSD([sQuery(id+"F0.wireOp",EDGE,"E61")])],"isStart":true})}),1.0]])]});
            var Q31;
            Q31=makeQuery(id+"F3.imprint","IMPRINT",FACE,{"disambiguationData":[TD([[makeQuery(id+"F3.imprint","IMPRINT",EDGE,{"derivedFrom":sQuery(id+"F3.wireOp",EDGE,"E246")}),1.0]])]});
            var Q32;
            Q32=makeQuery(id+"F3.imprint","IMPRINT",FACE,{"disambiguationData":[TD([[makeQuery(id+"F3.imprint","IMPRINT",EDGE,{"derivedFrom":makeQuery(id+"F1.opExtrude","CAP_EDGE",EDGE,{"disambiguationData":[OSD([sQuery(id+"F0.wireOp",EDGE,"E62")])],"isStart":true})}),1.0]])]});
            var Q33;
            Q33=makeQuery(id+"F3.imprint","IMPRINT",FACE,{"disambiguationData":[TD([[makeQuery(id+"F3.imprint","IMPRINT",EDGE,{"derivedFrom":makeQuery(id+"F1.opExtrude","CAP_EDGE",EDGE,{"disambiguationData":[OSD([sQuery(id+"F0.wireOp",EDGE,"E24")])],"isStart":true})}),1.0]])]});
            var Q34;
            Q34=makeQuery(id+"F3.imprint","IMPRINT",FACE,{"disambiguationData":[TD([[makeQuery(id+"F3.imprint","IMPRINT",EDGE,{"derivedFrom":sQuery(id+"F3.wireOp",EDGE,"E234")}),1.0]])]});
            var Q35;
            Q35=makeQuery(id+"F3.imprint","IMPRINT",FACE,{"disambiguationData":[TD([[makeQuery(id+"F3.imprint","IMPRINT",EDGE,{"derivedFrom":sQuery(id+"F3.wireOp",EDGE,"E233")}),1.0]])]});
            var Q36;
            Q36=makeQuery(id+"F3.imprint","IMPRINT",FACE,{"disambiguationData":[TD([[makeQuery(id+"F3.imprint","IMPRINT",EDGE,{"derivedFrom":makeQuery(id+"F1.opExtrude","CAP_EDGE",EDGE,{"disambiguationData":[OSD([sQuery(id+"F0.wireOp",EDGE,"E73.MirrorC")])],"isStart":true})}),-1.0]])]});
            var Q37;
            Q37=makeQuery(id+"F3.imprint","IMPRINT",FACE,{"disambiguationData":[TD([[makeQuery(id+"F3.imprint","IMPRINT",EDGE,{"derivedFrom":sQuery(id+"F3.wireOp",EDGE,"E249")}),1.0]])]});
            var Q38;
            Q38=makeQuery(id+"F3.imprint","IMPRINT",FACE,{"disambiguationData":[TD([[makeQuery(id+"F3.imprint","IMPRINT",EDGE,{"derivedFrom":makeQuery(id+"F1.opExtrude","CAP_EDGE",EDGE,{"disambiguationData":[OSD([sQuery(id+"F0.wireOp",EDGE,"E123")])],"isStart":true})}),1.0]])]});
            var Q39;
            Q39=makeQuery(id+"F3.imprint","IMPRINT",FACE,{"disambiguationData":[TD([[makeQuery(id+"F3.imprint","IMPRINT",EDGE,{"derivedFrom":sQuery(id+"F3.wireOp",EDGE,"E252")}),1.0]])]});
            var Q40;
            Q40=makeQuery(id+"F3.imprint","IMPRINT",FACE,{"disambiguationData":[TD([[makeQuery(id+"F3.imprint","IMPRINT",EDGE,{"derivedFrom":makeQuery(id+"F1.opExtrude","CAP_EDGE",EDGE,{"disambiguationData":[OSD([sQuery(id+"F0.wireOp",EDGE,"E143.MirrorC")])],"isStart":true})}),-1.0]])]});
            var Q41;
            Q41=makeQuery(id+"F3.imprint","IMPRINT",FACE,{"disambiguationData":[TD([[makeQuery(id+"F3.imprint","IMPRINT",EDGE,{"derivedFrom":makeQuery(id+"F1.opExtrude","CAP_EDGE",EDGE,{"disambiguationData":[OSD([sQuery(id+"F0.wireOp",EDGE,"E142")])],"isStart":true})}),1.0]])]});
            var Q42;
            Q42=makeQuery(id+"F3.imprint","IMPRINT",FACE,{"disambiguationData":[TD([[makeQuery(id+"F3.imprint","IMPRINT",EDGE,{"derivedFrom":sQuery(id+"F3.wireOp",EDGE,"E237")}),1.0]])]});
            extrude(context, id + "F4", {"entities" : qUnion([Q0, Q1, Q2, Q3, Q4, Q5, Q6, Q7, Q8, Q9, Q10, Q11, Q12, Q13, Q14, Q15, Q16, Q17, Q18, Q19, Q20, Q21, Q22, Q23, Q24, Q25, Q26, Q27, Q28, Q29, Q30, Q31, Q32, Q33, Q34, Q35, Q36, Q37, Q38, Q39, Q40, Q41, Q42]), "depth" : 13 * mm});
        }
        {
            var Q0;
            Q0=makeQuery(id+"F3.imprint","IMPRINT",FACE,{"disambiguationData":[TD([[makeQuery(id+"F3.imprint","IMPRINT",EDGE,{"derivedFrom":sQuery(id+"F3.wireOp",EDGE,"E219")}),1.0]])]});
            var Q1;
            Q1=makeQuery(id+"F3.imprint","IMPRINT",FACE,{"disambiguationData":[TD([[makeQuery(id+"F3.imprint","IMPRINT",EDGE,{"derivedFrom":sQuery(id+"F3.wireOp",EDGE,"E215")}),1.0]])]});
            var Q2;
            Q2=makeQuery(id+"F3.imprint","IMPRINT",FACE,{"disambiguationData":[TD([[makeQuery(id+"F3.imprint","IMPRINT",EDGE,{"derivedFrom":sQuery(id+"F3.wireOp",EDGE,"E216")}),1.0]])]});
            var Q3;
            Q3=makeQuery(id+"F3.imprint","IMPRINT",FACE,{"disambiguationData":[TD([[makeQuery(id+"F3.imprint","IMPRINT",EDGE,{"derivedFrom":sQuery(id+"F3.wireOp",EDGE,"E217")}),1.0]])]});
            var Q4;
            Q4=makeQuery(id+"F3.imprint","IMPRINT",FACE,{"disambiguationData":[TD([[makeQuery(id+"F3.imprint","IMPRINT",EDGE,{"derivedFrom":sQuery(id+"F3.wireOp",EDGE,"E218")}),1.0]])]});
            var Q5;
            Q5=makeQuery(id+"F3.imprint","IMPRINT",FACE,{"disambiguationData":[TD([[makeQuery(id+"F3.imprint","IMPRINT",EDGE,{"derivedFrom":sQuery(id+"F3.wireOp",EDGE,"E229")}),1.0]])]});
            var Q6;
            Q6=makeQuery(id+"F3.imprint","IMPRINT",FACE,{"disambiguationData":[TD([[makeQuery(id+"F3.imprint","IMPRINT",EDGE,{"derivedFrom":sQuery(id+"F3.wireOp",EDGE,"E228")}),1.0]])]});
            var Q7;
            Q7=makeQuery(id+"F3.imprint","IMPRINT",FACE,{"disambiguationData":[TD([[makeQuery(id+"F3.imprint","IMPRINT",EDGE,{"derivedFrom":sQuery(id+"F3.wireOp",EDGE,"E227")}),1.0]])]});
            var Q8;
            Q8=makeQuery(id+"F3.imprint","IMPRINT",FACE,{"disambiguationData":[TD([[makeQuery(id+"F3.imprint","IMPRINT",EDGE,{"derivedFrom":sQuery(id+"F3.wireOp",EDGE,"E226")}),1.0]])]});
            var Q9;
            Q9=makeQuery(id+"F3.imprint","IMPRINT",FACE,{"disambiguationData":[TD([[makeQuery(id+"F3.imprint","IMPRINT",EDGE,{"derivedFrom":sQuery(id+"F3.wireOp",EDGE,"E225")}),1.0]])]});
            var Q10;
            Q10=makeQuery(id+"F3.imprint","IMPRINT",FACE,{"disambiguationData":[TD([[makeQuery(id+"F3.imprint","IMPRINT",EDGE,{"derivedFrom":sQuery(id+"F3.wireOp",EDGE,"E224")}),1.0]])]});
            var Q11;
            Q11=makeQuery(id+"F3.imprint","IMPRINT",FACE,{"disambiguationData":[TD([[makeQuery(id+"F3.imprint","IMPRINT",EDGE,{"derivedFrom":sQuery(id+"F3.wireOp",EDGE,"E223")}),1.0]])]});
            var Q12;
            Q12=makeQuery(id+"F3.imprint","IMPRINT",FACE,{"disambiguationData":[TD([[makeQuery(id+"F3.imprint","IMPRINT",EDGE,{"derivedFrom":sQuery(id+"F3.wireOp",EDGE,"E231")}),1.0]])]});
            var Q13;
            Q13=makeQuery(id+"F3.imprint","IMPRINT",FACE,{"disambiguationData":[TD([[makeQuery(id+"F3.imprint","IMPRINT",EDGE,{"derivedFrom":sQuery(id+"F3.wireOp",EDGE,"E222")}),1.0]])]});
            var Q14;
            Q14=makeQuery(id+"F3.imprint","IMPRINT",FACE,{"disambiguationData":[TD([[makeQuery(id+"F3.imprint","IMPRINT",EDGE,{"derivedFrom":sQuery(id+"F3.wireOp",EDGE,"E221")}),1.0]])]});
            var Q15;
            Q15=makeQuery(id+"F3.imprint","IMPRINT",FACE,{"disambiguationData":[TD([[makeQuery(id+"F3.imprint","IMPRINT",EDGE,{"derivedFrom":sQuery(id+"F3.wireOp",EDGE,"E220")}),1.0]])]});
            var Q16;
            Q16=makeQuery(id+"F3.imprint","IMPRINT",FACE,{"disambiguationData":[TD([[makeQuery(id+"F3.imprint","IMPRINT",EDGE,{"derivedFrom":makeQuery(id+"F1.opExtrude","CAP_EDGE",EDGE,{"disambiguationData":[OSD([sQuery(id+"F0.wireOp",EDGE,"E17")])],"isStart":true})}),1.0]])]});
            var Q17;
            Q17=makeQuery(id+"F3.imprint","IMPRINT",FACE,{"disambiguationData":[TD([[makeQuery(id+"F3.imprint","IMPRINT",EDGE,{"derivedFrom":makeQuery(id+"F1.opExtrude","CAP_EDGE",EDGE,{"disambiguationData":[OSD([sQuery(id+"F0.wireOp",EDGE,"E18")])],"isStart":true})}),1.0]])]});
            var Q18;
            Q18=makeQuery(id+"F3.imprint","IMPRINT",FACE,{"disambiguationData":[TD([[makeQuery(id+"F3.imprint","IMPRINT",EDGE,{"derivedFrom":makeQuery(id+"F1.opExtrude","CAP_EDGE",EDGE,{"disambiguationData":[OSD([sQuery(id+"F0.wireOp",EDGE,"E19")])],"isStart":true})}),1.0]])]});
            var Q19;
            Q19=makeQuery(id+"F3.imprint","IMPRINT",FACE,{"disambiguationData":[TD([[makeQuery(id+"F3.imprint","IMPRINT",EDGE,{"derivedFrom":makeQuery(id+"F1.opExtrude","CAP_EDGE",EDGE,{"disambiguationData":[OSD([sQuery(id+"F0.wireOp",EDGE,"E20")])],"isStart":true})}),1.0]])]});
            var Q20;
            Q20=makeQuery(id+"F3.imprint","IMPRINT",FACE,{"disambiguationData":[TD([[makeQuery(id+"F3.imprint","IMPRINT",EDGE,{"derivedFrom":makeQuery(id+"F1.opExtrude","CAP_EDGE",EDGE,{"disambiguationData":[OSD([sQuery(id+"F0.wireOp",EDGE,"E74.MirrorC")])],"isStart":true})}),-1.0]])]});
            var Q21;
            Q21=makeQuery(id+"F3.imprint","IMPRINT",FACE,{"disambiguationData":[TD([[makeQuery(id+"F3.imprint","IMPRINT",EDGE,{"derivedFrom":makeQuery(id+"F1.opExtrude","CAP_EDGE",EDGE,{"disambiguationData":[OSD([sQuery(id+"F0.wireOp",EDGE,"E75.MirrorC")])],"isStart":true})}),-1.0]])]});
            var Q22;
            Q22=makeQuery(id+"F3.imprint","IMPRINT",FACE,{"disambiguationData":[TD([[makeQuery(id+"F3.imprint","IMPRINT",EDGE,{"derivedFrom":makeQuery(id+"F1.opExtrude","CAP_EDGE",EDGE,{"disambiguationData":[OSD([sQuery(id+"F0.wireOp",EDGE,"E76.MirrorC")])],"isStart":true})}),-1.0]])]});
            var Q23;
            Q23=makeQuery(id+"F3.imprint","IMPRINT",FACE,{"disambiguationData":[TD([[makeQuery(id+"F3.imprint","IMPRINT",EDGE,{"derivedFrom":sQuery(id+"F3.wireOp",EDGE,"E230")}),1.0]])]});
            var Q24;
            Q24=makeQuery(id+"F3.imprint","IMPRINT",FACE,{"disambiguationData":[TD([[makeQuery(id+"F3.imprint","IMPRINT",EDGE,{"derivedFrom":makeQuery(id+"F1.opExtrude","CAP_EDGE",EDGE,{"disambiguationData":[OSD([sQuery(id+"F0.wireOp",EDGE,"E63")])],"isStart":true})}),1.0]])]});
            var Q25;
            Q25=makeQuery(id+"F3.imprint","IMPRINT",FACE,{"disambiguationData":[TD([[makeQuery(id+"F3.imprint","IMPRINT",EDGE,{"derivedFrom":makeQuery(id+"F1.opExtrude","CAP_EDGE",EDGE,{"disambiguationData":[OSD([sQuery(id+"F0.wireOp",EDGE,"E78.MirrorC")])],"isStart":true})}),-1.0]])]});
            var Q26;
            Q26=makeQuery(id+"F3.imprint","IMPRINT",FACE,{"disambiguationData":[TD([[makeQuery(id+"F3.imprint","IMPRINT",EDGE,{"derivedFrom":makeQuery(id+"F1.opExtrude","CAP_EDGE",EDGE,{"disambiguationData":[OSD([sQuery(id+"F0.wireOp",EDGE,"E16")])],"isStart":true})}),1.0]])]});
            var Q27;
            Q27=makeQuery(id+"F3.imprint","IMPRINT",FACE,{"disambiguationData":[TD([[makeQuery(id+"F3.imprint","IMPRINT",EDGE,{"derivedFrom":makeQuery(id+"F1.opExtrude","CAP_EDGE",EDGE,{"disambiguationData":[OSD([sQuery(id+"F0.wireOp",EDGE,"E79.MirrorC")])],"isStart":true})}),-1.0]])]});
            var Q28;
            Q28=makeQuery(id+"F3.imprint","IMPRINT",FACE,{"disambiguationData":[TD([[makeQuery(id+"F3.imprint","IMPRINT",EDGE,{"derivedFrom":makeQuery(id+"F1.opExtrude","CAP_EDGE",EDGE,{"disambiguationData":[OSD([sQuery(id+"F0.wireOp",EDGE,"E82.MirrorC")])],"isStart":true})}),1.0]])]});
            var Q29;
            Q29=makeQuery(id+"F3.imprint","IMPRINT",FACE,{"disambiguationData":[TD([[makeQuery(id+"F3.imprint","IMPRINT",EDGE,{"derivedFrom":makeQuery(id+"F1.opExtrude","CAP_EDGE",EDGE,{"disambiguationData":[OSD([sQuery(id+"F0.wireOp",EDGE,"E83.MirrorC")])],"isStart":true})}),1.0]])]});
            var Q30;
            Q30=makeQuery(id+"F3.imprint","IMPRINT",FACE,{"disambiguationData":[TD([[makeQuery(id+"F3.imprint","IMPRINT",EDGE,{"derivedFrom":makeQuery(id+"F1.opExtrude","CAP_EDGE",EDGE,{"disambiguationData":[OSD([sQuery(id+"F0.wireOp",EDGE,"E80.MirrorC")])],"isStart":true})}),-1.0]])]});
            var Q31;
            Q31=makeQuery(id+"F3.imprint","IMPRINT",FACE,{"disambiguationData":[TD([[makeQuery(id+"F3.imprint","IMPRINT",EDGE,{"derivedFrom":makeQuery(id+"F1.opExtrude","CAP_EDGE",EDGE,{"disambiguationData":[OSD([sQuery(id+"F0.wireOp",EDGE,"E84.MirrorC")])],"isStart":true})}),1.0]])]});
            var Q32;
            Q32=makeQuery(id+"F3.imprint","IMPRINT",FACE,{"disambiguationData":[TD([[makeQuery(id+"F3.imprint","IMPRINT",EDGE,{"derivedFrom":makeQuery(id+"F1.opExtrude","CAP_EDGE",EDGE,{"disambiguationData":[OSD([sQuery(id+"F0.wireOp",EDGE,"E77.MirrorC")])],"isStart":true})}),-1.0]])]});
            var Q33;
            Q33=makeQuery(id+"F3.imprint","IMPRINT",FACE,{"disambiguationData":[TD([[makeQuery(id+"F3.imprint","IMPRINT",EDGE,{"derivedFrom":makeQuery(id+"F1.opExtrude","CAP_EDGE",EDGE,{"disambiguationData":[OSD([sQuery(id+"F0.wireOp",EDGE,"E81.MirrorC")])],"isStart":true})}),-1.0]])]});
            extrude(context, id + "F5", {"entities" : qUnion([Q0, Q1, Q2, Q3, Q4, Q5, Q6, Q7, Q8, Q9, Q10, Q11, Q12, Q13, Q14, Q15, Q16, Q17, Q18, Q19, Q20, Q21, Q22, Q23, Q24, Q25, Q26, Q27, Q28, Q29, Q30, Q31, Q32, Q33]), "depth" : 16 * mm});
        }
        {
            var Q0;
            Q0=makeQuery(id+"F3.imprint","IMPRINT",FACE,{"disambiguationData":[TD([[makeQuery(id+"F3.imprint","IMPRINT",EDGE,{"derivedFrom":makeQuery(id+"F1.opExtrude","CAP_EDGE",EDGE,{"disambiguationData":[OSD([sQuery(id+"F0.wireOp",EDGE,"E58")])],"isStart":true})}),1.0]])]});
            var Q1;
            Q1=makeQuery(id+"F3.imprint","IMPRINT",FACE,{"disambiguationData":[TD([[makeQuery(id+"F3.imprint","IMPRINT",EDGE,{"derivedFrom":makeQuery(id+"F1.opExtrude","CAP_EDGE",EDGE,{"disambiguationData":[OSD([sQuery(id+"F0.wireOp",EDGE,"E32")])],"isStart":true})}),1.0]])]});
            var Q2;
            Q2=makeQuery(id+"F3.imprint","IMPRINT",FACE,{"disambiguationData":[TD([[makeQuery(id+"F3.imprint","IMPRINT",EDGE,{"derivedFrom":makeQuery(id+"F1.opExtrude","CAP_EDGE",EDGE,{"disambiguationData":[OSD([sQuery(id+"F0.wireOp",EDGE,"E31")])],"isStart":true})}),1.0]])]});
            var Q3;
            Q3=makeQuery(id+"F3.imprint","IMPRINT",FACE,{"disambiguationData":[TD([[makeQuery(id+"F3.imprint","IMPRINT",EDGE,{"derivedFrom":makeQuery(id+"F1.opExtrude","CAP_EDGE",EDGE,{"disambiguationData":[OSD([sQuery(id+"F0.wireOp",EDGE,"E30")])],"isStart":true})}),1.0]])]});
            var Q4;
            Q4=makeQuery(id+"F3.imprint","IMPRINT",FACE,{"disambiguationData":[TD([[makeQuery(id+"F3.imprint","IMPRINT",EDGE,{"derivedFrom":makeQuery(id+"F1.opExtrude","CAP_EDGE",EDGE,{"disambiguationData":[OSD([sQuery(id+"F0.wireOp",EDGE,"E101.MirrorC")])],"isStart":true})}),-1.0]])]});
            var Q5;
            Q5=makeQuery(id+"F3.imprint","IMPRINT",FACE,{"disambiguationData":[TD([[makeQuery(id+"F3.imprint","IMPRINT",EDGE,{"derivedFrom":makeQuery(id+"F1.opExtrude","CAP_EDGE",EDGE,{"disambiguationData":[OSD([sQuery(id+"F0.wireOp",EDGE,"E102.MirrorC")])],"isStart":true})}),-1.0]])]});
            var Q6;
            Q6=makeQuery(id+"F3.imprint","IMPRINT",FACE,{"disambiguationData":[TD([[makeQuery(id+"F3.imprint","IMPRINT",EDGE,{"derivedFrom":makeQuery(id+"F1.opExtrude","CAP_EDGE",EDGE,{"disambiguationData":[OSD([sQuery(id+"F0.wireOp",EDGE,"E42")])],"isStart":true})}),1.0]])]});
            var Q7;
            Q7=makeQuery(id+"F3.imprint","IMPRINT",FACE,{"disambiguationData":[TD([[makeQuery(id+"F3.imprint","IMPRINT",EDGE,{"derivedFrom":makeQuery(id+"F1.opExtrude","CAP_EDGE",EDGE,{"disambiguationData":[OSD([sQuery(id+"F0.wireOp",EDGE,"E92.MirrorC")])],"isStart":true})}),-1.0]])]});
            var Q8;
            Q8=makeQuery(id+"F3.imprint","IMPRINT",FACE,{"disambiguationData":[TD([[makeQuery(id+"F3.imprint","IMPRINT",EDGE,{"derivedFrom":makeQuery(id+"F1.opExtrude","CAP_EDGE",EDGE,{"disambiguationData":[OSD([sQuery(id+"F0.wireOp",EDGE,"E93.MirrorC")])],"isStart":true})}),-1.0]])]});
            var Q9;
            Q9=makeQuery(id+"F3.imprint","IMPRINT",FACE,{"disambiguationData":[TD([[makeQuery(id+"F3.imprint","IMPRINT",EDGE,{"derivedFrom":makeQuery(id+"F1.opExtrude","CAP_EDGE",EDGE,{"disambiguationData":[OSD([sQuery(id+"F0.wireOp",EDGE,"E94.MirrorC")])],"isStart":true})}),-1.0]])]});
            var Q10;
            Q10=makeQuery(id+"F3.imprint","IMPRINT",FACE,{"disambiguationData":[TD([[makeQuery(id+"F3.imprint","IMPRINT",EDGE,{"derivedFrom":makeQuery(id+"F1.opExtrude","CAP_EDGE",EDGE,{"disambiguationData":[OSD([sQuery(id+"F0.wireOp",EDGE,"E95.MirrorC")])],"isStart":true})}),-1.0]])]});
            var Q11;
            Q11=makeQuery(id+"F3.imprint","IMPRINT",FACE,{"disambiguationData":[TD([[makeQuery(id+"F3.imprint","IMPRINT",EDGE,{"derivedFrom":makeQuery(id+"F1.opExtrude","CAP_EDGE",EDGE,{"disambiguationData":[OSD([sQuery(id+"F0.wireOp",EDGE,"E110.MirrorC")])],"isStart":true})}),1.0]])]});
            var Q12;
            Q12=makeQuery(id+"F3.imprint","IMPRINT",FACE,{"disambiguationData":[TD([[makeQuery(id+"F3.imprint","IMPRINT",EDGE,{"derivedFrom":makeQuery(id+"F1.opExtrude","CAP_EDGE",EDGE,{"disambiguationData":[OSD([sQuery(id+"F0.wireOp",EDGE,"E107.MirrorC")])],"isStart":true})}),1.0]])]});
            var Q13;
            Q13=makeQuery(id+"F3.imprint","IMPRINT",FACE,{"disambiguationData":[TD([[makeQuery(id+"F3.imprint","IMPRINT",EDGE,{"derivedFrom":makeQuery(id+"F1.opExtrude","CAP_EDGE",EDGE,{"disambiguationData":[OSD([sQuery(id+"F0.wireOp",EDGE,"E106.MirrorC")])],"isStart":true})}),1.0]])]});
            var Q14;
            Q14=makeQuery(id+"F3.imprint","IMPRINT",FACE,{"disambiguationData":[TD([[makeQuery(id+"F3.imprint","IMPRINT",EDGE,{"derivedFrom":makeQuery(id+"F1.opExtrude","CAP_EDGE",EDGE,{"disambiguationData":[OSD([sQuery(id+"F0.wireOp",EDGE,"E111.MirrorC")])],"isStart":true})}),-1.0]])]});
            var Q15;
            Q15=makeQuery(id+"F3.imprint","IMPRINT",FACE,{"disambiguationData":[TD([[makeQuery(id+"F3.imprint","IMPRINT",EDGE,{"derivedFrom":makeQuery(id+"F1.opExtrude","CAP_EDGE",EDGE,{"disambiguationData":[OSD([sQuery(id+"F0.wireOp",EDGE,"E105.MirrorC")])],"isStart":true})}),-1.0]])]});
            var Q16;
            Q16=makeQuery(id+"F3.imprint","IMPRINT",FACE,{"disambiguationData":[TD([[makeQuery(id+"F3.imprint","IMPRINT",EDGE,{"derivedFrom":makeQuery(id+"F1.opExtrude","CAP_EDGE",EDGE,{"disambiguationData":[OSD([sQuery(id+"F0.wireOp",EDGE,"E125")])],"isStart":true})}),1.0]])]});
            var Q17;
            Q17=makeQuery(id+"F3.imprint","IMPRINT",FACE,{"disambiguationData":[TD([[makeQuery(id+"F3.imprint","IMPRINT",EDGE,{"derivedFrom":sQuery(id+"F3.wireOp",EDGE,"E250.0")}),1.0]])]});
            var Q18;
            Q18=makeQuery(id+"F3.imprint","IMPRINT",FACE,{"disambiguationData":[TD([[makeQuery(id+"F3.imprint","IMPRINT",EDGE,{"derivedFrom":sQuery(id+"F3.wireOp",EDGE,"E251.0")}),1.0]])]});
            extrude(context, id + "F6", {"entities" : qUnion([Q0, Q1, Q2, Q3, Q4, Q5, Q6, Q7, Q8, Q9, Q10, Q11, Q12, Q13, Q14, Q15, Q16, Q17, Q18]), "depth" : 1 * mm});
        }
        {
            var Q0;
            Q0=makeQuery(id+"F1.opExtrude","CAP_FACE",FACE,{"disambiguationData":[OSD([sQuery(id+"F0.wireOp",EDGE,"E0.bottom"),sQuery(id+"F0.wireOp",EDGE,"E0.top"),sQuery(id+"F0.wireOp",EDGE,"E0.left"),sQuery(id+"F0.wireOp",EDGE,"E0.right"),sQuery(id+"F0.wireOp",EDGE,"E16"),sQuery(id+"F0.wireOp",EDGE,"E17"),sQuery(id+"F0.wireOp",EDGE,"E18"),sQuery(id+"F0.wireOp",EDGE,"E19"),sQuery(id+"F0.wireOp",EDGE,"E20"),sQuery(id+"F0.wireOp",EDGE,"E24"),sQuery(id+"F0.wireOp",EDGE,"E25"),sQuery(id+"F0.wireOp",EDGE,"E26"),sQuery(id+"F0.wireOp",EDGE,"E30"),sQuery(id+"F0.wireOp",EDGE,"E31"),sQuery(id+"F0.wireOp",EDGE,"E32"),sQuery(id+"F0.wireOp",EDGE,"E37"),sQuery(id+"F0.wireOp",EDGE,"E47"),sQuery(id+"F0.wireOp",EDGE,"E49"),sQuery(id+"F0.wireOp",EDGE,"E50"),sQuery(id+"F0.wireOp",EDGE,"E51"),sQuery(id+"F0.wireOp",EDGE,"E57"),sQuery(id+"F0.wireOp",EDGE,"E58"),sQuery(id+"F0.wireOp",EDGE,"E61"),sQuery(id+"F0.wireOp",EDGE,"E62"),sQuery(id+"F0.wireOp",EDGE,"E63"),sQuery(id+"F0.wireOp",EDGE,"E64"),sQuery(id+"F0.wireOp",EDGE,"E65"),sQuery(id+"F0.wireOp",EDGE,"E66"),sQuery(id+"F0.wireOp",EDGE,"E70.MirrorC"),sQuery(id+"F0.wireOp",EDGE,"E71.MirrorC"),sQuery(id+"F0.wireOp",EDGE,"E72.MirrorC"),sQuery(id+"F0.wireOp",EDGE,"E73.MirrorC"),sQuery(id+"F0.wireOp",EDGE,"E74.MirrorC"),sQuery(id+"F0.wireOp",EDGE,"E75.MirrorC"),sQuery(id+"F0.wireOp",EDGE,"E77.MirrorC"),sQuery(id+"F0.wireOp",EDGE,"E76.MirrorC"),sQuery(id+"F0.wireOp",EDGE,"E78.MirrorC"),sQuery(id+"F0.wireOp",EDGE,"E79.MirrorC"),sQuery(id+"F0.wireOp",EDGE,"E80.MirrorC"),sQuery(id+"F0.wireOp",EDGE,"E81.MirrorC"),sQuery(id+"F0.wireOp",EDGE,"E82.MirrorC"),sQuery(id+"F0.wireOp",EDGE,"E83.MirrorC"),sQuery(id+"F0.wireOp",EDGE,"E84.MirrorC"),sQuery(id+"F0.wireOp",EDGE,"E85.MirrorC"),sQuery(id+"F0.wireOp",EDGE,"E86.MirrorC"),sQuery(id+"F0.wireOp",EDGE,"E87.MirrorC"),sQuery(id+"F0.wireOp",EDGE,"E88.MirrorC"),sQuery(id+"F0.wireOp",EDGE,"E89.MirrorC"),sQuery(id+"F0.wireOp",EDGE,"E90.MirrorC"),sQuery(id+"F0.wireOp",EDGE,"E91.MirrorC"),sQuery(id+"F0.wireOp",EDGE,"E92.MirrorC"),sQuery(id+"F0.wireOp",EDGE,"E93.MirrorC"),sQuery(id+"F0.wireOp",EDGE,"E94.MirrorC"),sQuery(id+"F0.wireOp",EDGE,"E95.MirrorC"),sQuery(id+"F0.wireOp",EDGE,"E96.MirrorC"),sQuery(id+"F0.wireOp",EDGE,"E97.MirrorC"),sQuery(id+"F0.wireOp",EDGE,"E98.MirrorC"),sQuery(id+"F0.wireOp",EDGE,"E99.MirrorC"),sQuery(id+"F0.wireOp",EDGE,"E100.MirrorC"),sQuery(id+"F0.wireOp",EDGE,"E101.MirrorC"),sQuery(id+"F0.wireOp",EDGE,"E102.MirrorC"),sQuery(id+"F0.wireOp",EDGE,"E103.MirrorC"),sQuery(id+"F0.wireOp",EDGE,"E104.MirrorC"),sQuery(id+"F0.wireOp",EDGE,"E105.MirrorC"),sQuery(id+"F0.wireOp",EDGE,"E106.MirrorC"),sQuery(id+"F0.wireOp",EDGE,"E107.MirrorC"),sQuery(id+"F0.wireOp",EDGE,"E108.MirrorC"),sQuery(id+"F0.wireOp",EDGE,"E109.MirrorC"),sQuery(id+"F0.wireOp",EDGE,"E110.MirrorC"),sQuery(id+"F0.wireOp",EDGE,"E113.MirrorC"),sQuery(id+"F0.wireOp",EDGE,"E114.MirrorC"),sQuery(id+"F0.wireOp",EDGE,"E115.MirrorC"),sQuery(id+"F0.wireOp",EDGE,"E116.MirrorC"),sQuery(id+"F0.wireOp",EDGE,"E117"),sQuery(id+"F0.wireOp",EDGE,"E118"),sQuery(id+"F0.wireOp",EDGE,"E119"),sQuery(id+"F0.wireOp",EDGE,"E120"),sQuery(id+"F0.wireOp",EDGE,"E121"),sQuery(id+"F0.wireOp",EDGE,"E122"),sQuery(id+"F0.wireOp",EDGE,"E123"),sQuery(id+"F0.wireOp",EDGE,"E124"),sQuery(id+"F0.wireOp",EDGE,"E125"),sQuery(id+"F0.wireOp",EDGE,"E131"),sQuery(id+"F0.wireOp",EDGE,"E132"),sQuery(id+"F0.wireOp",EDGE,"E133")])],"isStart":true});
            var sketch = newSketch(context, id + "F7", { "sketchPlane" : qUnion([Q0])});
            skSolve(sketch);
        }
        {
            var Q0;
            Q0=makeQuery(id+"F7.imprint","IMPRINT",FACE,{"disambiguationData":[TD([[makeQuery(id+"F7.imprint","IMPRINT",EDGE,{"derivedFrom":makeQuery(id+"F1.opExtrude","CAP_EDGE",EDGE,{"disambiguationData":[OSD([sQuery(id+"F0.wireOp",EDGE,"E0.bottom")])],"isStart":true})}),1.0]])]});
            var sketch = newSketch(context, id + "F8", { "sketchPlane" : qUnion([Q0])});
            skCircle(sketch, "E253", {"center": v(6.35, 214.67) * mm, "radius": 2.75 * mm});
            skCircle(sketch, "E254", {"center": v(304.8, 214.67) * mm, "radius": 2.75 * mm});
            skCircle(sketch, "E255", {"center": v(304.8, 6.35) * mm, "radius": 2.75 * mm});
            skCircle(sketch, "E256", {"center": v(6.35, 6.35) * mm, "radius": 2.75 * mm});
            skCircle(sketch, "E257.0", {"center": v(155.57, 116.47) * mm, "radius": 13.5 * mm});
            skLineSegment(sketch, "E258", {"start": v(155.57, 116.47) * mm, "end": v(155.57, 214.67) * mm, "construction": true});
            skSolve(sketch);
        }
        {
            var Q0;
            Q0=makeQuery(id+"F8.imprint","IMPRINT",FACE,{"disambiguationData":[TD([[makeQuery(id+"F8.imprint","IMPRINT",EDGE,{"derivedFrom":sQuery(id+"F8.wireOp",EDGE,"E253")}),1.0]])]});
            var Q1;
            Q1=makeQuery(id+"F8.imprint","IMPRINT",FACE,{"disambiguationData":[TD([[makeQuery(id+"F8.imprint","IMPRINT",EDGE,{"derivedFrom":sQuery(id+"F8.wireOp",EDGE,"E256")}),1.0]])]});
            var Q2;
            Q2=makeQuery(id+"F8.imprint","IMPRINT",FACE,{"disambiguationData":[TD([[makeQuery(id+"F8.imprint","IMPRINT",EDGE,{"derivedFrom":sQuery(id+"F8.wireOp",EDGE,"E255")}),1.0]])]});
            var Q3;
            Q3=makeQuery(id+"F8.imprint","IMPRINT",FACE,{"disambiguationData":[TD([[makeQuery(id+"F8.imprint","IMPRINT",EDGE,{"derivedFrom":sQuery(id+"F8.wireOp",EDGE,"E254")}),1.0]])]});
            extrude(context, id + "F9", {"entities" : qUnion([Q0, Q1, Q2, Q3]), "operationType" : NewBodyOperationType.REMOVE, "endBound" : BoundingType.THROUGH_ALL, "oppositeDirection" : true, "depth" : 25 * mm});
        }
        {
            var Q0;
            Q0=makeQuery(id+"F1.opExtrude","CAP_FACE",FACE,{"disambiguationData":[OSD([sQuery(id+"F0.wireOp",EDGE,"E0.bottom"),sQuery(id+"F0.wireOp",EDGE,"E0.top"),sQuery(id+"F0.wireOp",EDGE,"E0.left"),sQuery(id+"F0.wireOp",EDGE,"E0.right"),sQuery(id+"F0.wireOp",EDGE,"E16"),sQuery(id+"F0.wireOp",EDGE,"E17"),sQuery(id+"F0.wireOp",EDGE,"E18"),sQuery(id+"F0.wireOp",EDGE,"E19"),sQuery(id+"F0.wireOp",EDGE,"E20"),sQuery(id+"F0.wireOp",EDGE,"E24"),sQuery(id+"F0.wireOp",EDGE,"E25"),sQuery(id+"F0.wireOp",EDGE,"E26"),sQuery(id+"F0.wireOp",EDGE,"E30"),sQuery(id+"F0.wireOp",EDGE,"E31"),sQuery(id+"F0.wireOp",EDGE,"E32"),sQuery(id+"F0.wireOp",EDGE,"E47"),sQuery(id+"F0.wireOp",EDGE,"E49"),sQuery(id+"F0.wireOp",EDGE,"E50"),sQuery(id+"F0.wireOp",EDGE,"E51"),sQuery(id+"F0.wireOp",EDGE,"E57"),sQuery(id+"F0.wireOp",EDGE,"E58"),sQuery(id+"F0.wireOp",EDGE,"E61"),sQuery(id+"F0.wireOp",EDGE,"E62"),sQuery(id+"F0.wireOp",EDGE,"E63"),sQuery(id+"F0.wireOp",EDGE,"E64"),sQuery(id+"F0.wireOp",EDGE,"E65"),sQuery(id+"F0.wireOp",EDGE,"E66"),sQuery(id+"F0.wireOp",EDGE,"E67"),sQuery(id+"F0.wireOp",EDGE,"E71.MirrorC"),sQuery(id+"F0.wireOp",EDGE,"E72.MirrorC"),sQuery(id+"F0.wireOp",EDGE,"E73.MirrorC"),sQuery(id+"F0.wireOp",EDGE,"E74.MirrorC"),sQuery(id+"F0.wireOp",EDGE,"E75.MirrorC"),sQuery(id+"F0.wireOp",EDGE,"E77.MirrorC"),sQuery(id+"F0.wireOp",EDGE,"E76.MirrorC"),sQuery(id+"F0.wireOp",EDGE,"E78.MirrorC"),sQuery(id+"F0.wireOp",EDGE,"E79.MirrorC"),sQuery(id+"F0.wireOp",EDGE,"E80.MirrorC"),sQuery(id+"F0.wireOp",EDGE,"E81.MirrorC"),sQuery(id+"F0.wireOp",EDGE,"E82.MirrorC"),sQuery(id+"F0.wireOp",EDGE,"E83.MirrorC"),sQuery(id+"F0.wireOp",EDGE,"E84.MirrorC"),sQuery(id+"F0.wireOp",EDGE,"E85.MirrorC"),sQuery(id+"F0.wireOp",EDGE,"E86.MirrorC"),sQuery(id+"F0.wireOp",EDGE,"E87.MirrorC"),sQuery(id+"F0.wireOp",EDGE,"E88.MirrorC"),sQuery(id+"F0.wireOp",EDGE,"E89.MirrorC"),sQuery(id+"F0.wireOp",EDGE,"E90.MirrorC"),sQuery(id+"F0.wireOp",EDGE,"E91.MirrorC"),sQuery(id+"F0.wireOp",EDGE,"E92.MirrorC"),sQuery(id+"F0.wireOp",EDGE,"E93.MirrorC"),sQuery(id+"F0.wireOp",EDGE,"E94.MirrorC"),sQuery(id+"F0.wireOp",EDGE,"E95.MirrorC"),sQuery(id+"F0.wireOp",EDGE,"E96.MirrorC"),sQuery(id+"F0.wireOp",EDGE,"E97.MirrorC"),sQuery(id+"F0.wireOp",EDGE,"E98.MirrorC"),sQuery(id+"F0.wireOp",EDGE,"E99.MirrorC"),sQuery(id+"F0.wireOp",EDGE,"E100.MirrorC"),sQuery(id+"F0.wireOp",EDGE,"E101.MirrorC"),sQuery(id+"F0.wireOp",EDGE,"E102.MirrorC"),sQuery(id+"F0.wireOp",EDGE,"E103.MirrorC"),sQuery(id+"F0.wireOp",EDGE,"E104.MirrorC"),sQuery(id+"F0.wireOp",EDGE,"E105.MirrorC"),sQuery(id+"F0.wireOp",EDGE,"E106.MirrorC"),sQuery(id+"F0.wireOp",EDGE,"E107.MirrorC"),sQuery(id+"F0.wireOp",EDGE,"E108.MirrorC"),sQuery(id+"F0.wireOp",EDGE,"E109.MirrorC"),sQuery(id+"F0.wireOp",EDGE,"E110.MirrorC"),sQuery(id+"F0.wireOp",EDGE,"E113.MirrorC"),sQuery(id+"F0.wireOp",EDGE,"E114.MirrorC"),sQuery(id+"F0.wireOp",EDGE,"E116.MirrorC"),sQuery(id+"F0.wireOp",EDGE,"E117"),sQuery(id+"F0.wireOp",EDGE,"E118"),sQuery(id+"F0.wireOp",EDGE,"E119"),sQuery(id+"F0.wireOp",EDGE,"E120"),sQuery(id+"F0.wireOp",EDGE,"E121"),sQuery(id+"F0.wireOp",EDGE,"E122"),sQuery(id+"F0.wireOp",EDGE,"E123"),sQuery(id+"F0.wireOp",EDGE,"E124"),sQuery(id+"F0.wireOp",EDGE,"E125"),sQuery(id+"F0.wireOp",EDGE,"E126"),sQuery(id+"F0.wireOp",EDGE,"E132"),sQuery(id+"F0.wireOp",EDGE,"E142"),sQuery(id+"F0.wireOp",EDGE,"E133"),sQuery(id+"F0.wireOp",EDGE,"E143.MirrorC")])],"isStart":false});
            var sketch = newSketch(context, id + "F10", { "sketchPlane" : qUnion([Q0])});
            skCircle(sketch, "E259", {"center": v(-155.57, 204.32) * mm, "radius": 15 * mm, "construction": true});
            skLineSegment(sketch, "E260.bottom", {"start": v(-162.57, 218.82) * mm, "end": v(-148.58, 218.82) * mm});
            skLineSegment(sketch, "E260.top", {"start": v(-162.57, 189.82) * mm, "end": v(-148.58, 189.82) * mm});
            skLineSegment(sketch, "E260.left", {"start": v(-170.57, 210.82) * mm, "end": v(-170.57, 197.82) * mm});
            skLineSegment(sketch, "E260.right", {"start": v(-140.58, 210.82) * mm, "end": v(-140.58, 197.82) * mm});
            skLineSegment(sketch, "E261", {"start": v(-155.57, 204.32) * mm, "end": v(-155.57, 218.82) * mm});
            skLineSegment(sketch, "E262", {"start": v(-155.57, 204.32) * mm, "end": v(-155.57, 189.82) * mm});
            skCircle(sketch, "E263", {"center": v(-273.7, 157.41) * mm, "radius": 16 * mm, "construction": true});
            skLineSegment(sketch, "E264", {"start": v(-162.57, 218.82) * mm, "end": v(-170.57, 210.82) * mm});
            skLineSegment(sketch, "E265", {"start": v(-170.57, 197.82) * mm, "end": v(-162.57, 189.82) * mm});
            skLineSegment(sketch, "E266", {"start": v(-148.58, 218.82) * mm, "end": v(-140.58, 210.82) * mm});
            skLineSegment(sketch, "E267", {"start": v(-140.58, 197.82) * mm, "end": v(-148.58, 189.82) * mm});
            skPoint(sketch, "E268.orphan", {"position": v(-170.57, 218.82) * mm});
            skPoint(sketch, "E269.orphan", {"position": v(-170.57, 189.82) * mm});
            skPoint(sketch, "E270.orphan", {"position": v(-140.58, 189.82) * mm});
            skPoint(sketch, "E271.orphan", {"position": v(-140.58, 218.82) * mm});
            skCircle(sketch, "E272", {"center": v(-155.57, 173.32) * mm, "radius": 16 * mm, "construction": true});
            skSolve(sketch);
        }
        {
            var Q0;
            Q0=makeQuery(id+"F10.imprint","IMPRINT",FACE,{"disambiguationData":[TD([[makeQuery(id+"F10.imprint","IMPRINT",EDGE,{"derivedFrom":sQuery(id+"F10.wireOp",EDGE,"E260.right")}),-1.0]])]});
            var Q1;
            Q1=makeQuery(id+"F10.imprint","IMPRINT",FACE,{"disambiguationData":[TD([[makeQuery(id+"F10.imprint","IMPRINT",EDGE,{"derivedFrom":sQuery(id+"F10.wireOp",EDGE,"E260.left")}),1.0]])]});
            var Q2;
            Q2=sQuery(id+"F10.wireOp",EDGE,"E272");
            extrude(context, id + "F11", {"entities" : qUnion([Q0, Q1]), "surfaceEntities" : qUnion([Q2]), "depth" : 25 * mm});
        }
    });
